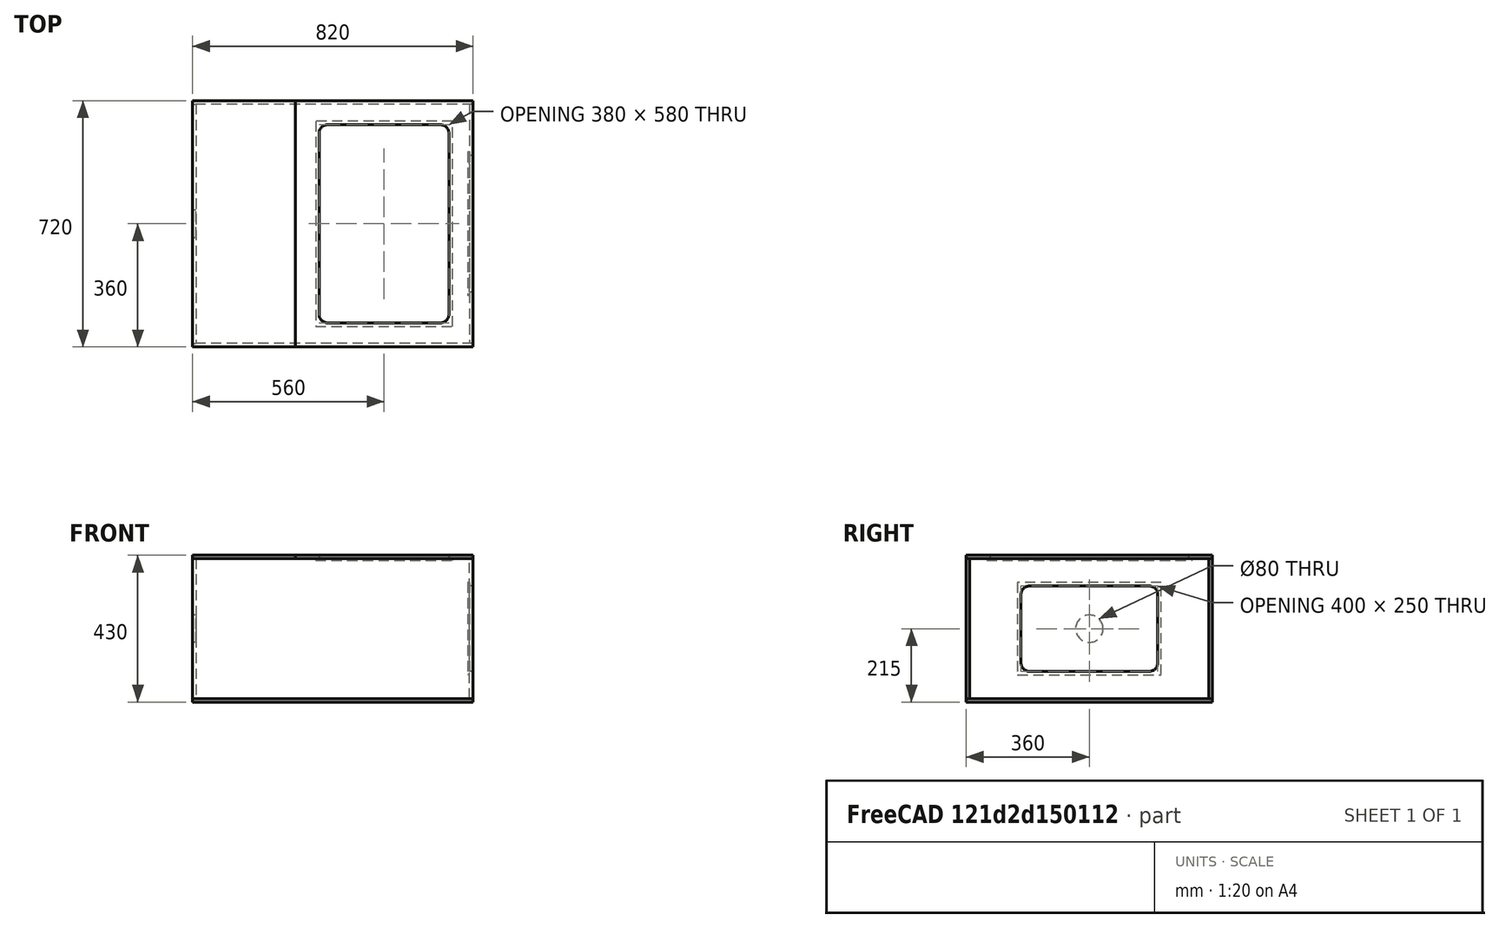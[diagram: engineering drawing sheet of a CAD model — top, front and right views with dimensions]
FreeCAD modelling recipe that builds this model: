
FCSTD DOCUMENT  (FreeCAD 0.19R24276 (Git))
Label: laser_cutter_enclosure
License: All rights reserved
LicenseURL: http://en.wikipedia.org/wiki/All_rights_reserved
objects: TechDraw::DrawProjGroupItem×81, TechDraw::DrawViewDimension×23, Sketcher::SketchObject×12, PartDesign::Pad×9, PartDesign::Body×9, TechDraw::DrawSVGTemplate×9, TechDraw::DrawProjGroup×9, TechDraw::DrawPage×9, PartDesign::ShapeBinder×8, PartDesign::Pocket×3
note: 53 computed .brp shape members not serialized (recipe doc carries the construction recipe); baked Part::Feature solids carry a one-line shape summary decoded from their .brp

FEATURE [Sketcher::SketchObject] Sketch
  FullyConstrained = true
  MapMode = 5
  Support = -> [XY_Plane]
  sketch-geometry (4):
    g0: LineSegment StartX=-410 StartY=360 StartZ=0 EndX=410 EndY=360 EndZ=0
    g1: LineSegment StartX=410 StartY=360 StartZ=0 EndX=410 EndY=-360 EndZ=0
    g2: LineSegment StartX=410 StartY=-360 StartZ=0 EndX=-410 EndY=-360 EndZ=0
    g3: LineSegment StartX=-410 StartY=-360 StartZ=0 EndX=-410 EndY=360 EndZ=0
  constraints (11):
    c: Coincident(g0,g1)
    c: Coincident(g1,g2)
    c: Coincident(g2,g3)
    c: Coincident(g3,g0)
    c: Horizontal(g0)
    c: Horizontal(g2)
    c: Vertical(g1)
    c: Vertical(g3)
    c: Symmetric(g0,g2,g-1)
    c: DistanceX(g0,g0) = 820
    c: DistanceY(g1,g1) = 720
FEATURE [PartDesign::Pad] Pad  label="bottom001"
  Direction = (1,1,1)
  Length = 10
  Length2 = 100
  Profile = -> Sketch
  Type = 0
FEATURE [PartDesign::Body] Body  label="bottom"
  Group = -> [Sketch,Pad]
  Origin = -> Origin
  Tip = -> Pad
FEATURE [PartDesign::ShapeBinder] CopyPad
  Placement = pos=(0,0,10) rot=(0,0,1;0rad)
  TraceSupport = false
FEATURE [Sketcher::SketchObject] Sketch001
  ExternalGeometry = -> [CopyPad]
  FullyConstrained = true
  MapMode = 5
  Placement = pos=(0,0,10) rot=(0,0,1;0rad)
  Support = -> [CopyPad]
  sketch-geometry (4):
    g0: LineSegment StartX=-410 StartY=360 StartZ=0 EndX=410 EndY=360 EndZ=0
    g1: LineSegment StartX=410 StartY=360 StartZ=0 EndX=410 EndY=350 EndZ=0
    g2: LineSegment StartX=410 StartY=350 StartZ=0 EndX=-410 EndY=350 EndZ=0
    g3: LineSegment StartX=-410 StartY=350 StartZ=0 EndX=-410 EndY=360 EndZ=0
  constraints (10):
    c: Coincident(g0,g1)
    c: Coincident(g1,g2)
    c: Coincident(g2,g3)
    c: Coincident(g3,g0)
    c: Horizontal(g2)
    c: Vertical(g1)
    c: Vertical(g3)
    c: Coincident(g0,g-3)
    c: Coincident(g0,g-3)
    c: DistanceY(g1,g1) = 10
FEATURE [PartDesign::Pad] Pad001  label="right_side001"
  Direction = (1,1,1)
  Length = 410
  Length2 = 100
  Placement = pos=(0,0,10) rot=(0,0,1;0rad)
  Profile = -> Sketch001
  Type = 0
FEATURE [PartDesign::Body] Body001  label="right_side"
  Group = -> [CopyPad,Sketch001,Pad001]
  Origin = -> Origin001
  Tip = -> Pad001
FEATURE [PartDesign::ShapeBinder] CopyPad001
  Placement = pos=(0,0,10) rot=(0,0,1;0rad)
  TraceSupport = false
FEATURE [Sketcher::SketchObject] Sketch002
  ExternalGeometry = -> [CopyPad001]
  FullyConstrained = true
  MapMode = 5
  Placement = pos=(0,0,10) rot=(0,0,1;0rad)
  Support = -> [CopyPad001]
  sketch-geometry (4):
    g0: LineSegment StartX=-410 StartY=-360 StartZ=0 EndX=410 EndY=-360 EndZ=0
    g1: LineSegment StartX=410 StartY=-360 StartZ=0 EndX=410 EndY=-350 EndZ=0
    g2: LineSegment StartX=410 StartY=-350 StartZ=0 EndX=-410 EndY=-350 EndZ=0
    g3: LineSegment StartX=-410 StartY=-350 StartZ=0 EndX=-410 EndY=-360 EndZ=0
  constraints (11):
    c: Coincident(g0,g1)
    c: Coincident(g1,g2)
    c: Coincident(g2,g3)
    c: Coincident(g3,g0)
    c: Horizontal(g0)
    c: Horizontal(g2)
    c: Vertical(g1)
    c: Vertical(g3)
    c: Coincident(g0,g-3)
    c: PointOnObject(g1,g-4)
    c: DistanceY(g1,g1) = 10
FEATURE [PartDesign::Pad] Pad002  label="left_side001"
  Direction = (1,1,1)
  Length = 410
  Length2 = 100
  Placement = pos=(0,0,10) rot=(0,0,1;0rad)
  Profile = -> Sketch002
  Type = 0
FEATURE [PartDesign::Body] Body002  label="left_side"
  Group = -> [CopyPad001,Sketch002,Pad002]
  Origin = -> Origin002
  Tip = -> Pad002
FEATURE [PartDesign::ShapeBinder] CopyPad002
  Placement = pos=(0,0,410) rot=(0,0,1;0rad)
  TraceSupport = false
FEATURE [Sketcher::SketchObject] Sketch003
  ExternalGeometry = -> [CopyPad002]
  FullyConstrained = true
  MapMode = 5
  Placement = pos=(0,0,420) rot=(0,0,1;0rad)
  Support = -> [CopyPad002]
  sketch-geometry (4):
    g0: LineSegment StartX=-410 StartY=-360 StartZ=0 EndX=-110 EndY=-360 EndZ=0
    g1: LineSegment StartX=-110 StartY=-360 StartZ=0 EndX=-110 EndY=360 EndZ=0
    g2: LineSegment StartX=-110 StartY=360 StartZ=0 EndX=-410 EndY=360 EndZ=0
    g3: LineSegment StartX=-410 StartY=360 StartZ=0 EndX=-410 EndY=-360 EndZ=0
  constraints (11):
    c: Coincident(g0,g1)
    c: Coincident(g1,g2)
    c: Coincident(g2,g3)
    c: Coincident(g3,g0)
    c: Horizontal(g0)
    c: Horizontal(g2)
    c: Vertical(g1)
    c: Vertical(g3)
    c: Coincident(g0,g-3)
    c: DistanceX(g2,g2) = 300
    c: DistanceY(g1,g1) = 720
FEATURE [PartDesign::Pad] Pad003  label="fixed_top_part001"
  Direction = (1,1,1)
  Length = 10
  Length2 = 100
  Placement = pos=(0,0,410) rot=(0,0,1;0rad)
  Profile = -> Sketch003
  Type = 0
FEATURE [PartDesign::Body] Body003  label="fixed_top_part"
  Group = -> [CopyPad002,Sketch003,Pad003]
  Origin = -> Origin003
  Tip = -> Pad003
FEATURE [PartDesign::ShapeBinder] CopyPad002001
  Placement = pos=(0,0,410) rot=(0,0,1;0rad)
  TraceSupport = false
FEATURE [Sketcher::SketchObject] Sketch004
  ExternalGeometry = -> [CopyPad002001]
  FullyConstrained = true
  MapMode = 5
  Placement = pos=(0,0,420) rot=(0,0,1;0rad)
  Support = -> [CopyPad002001]
  sketch-geometry (4):
    g0: LineSegment StartX=410 StartY=-360 StartZ=0 EndX=-110 EndY=-360 EndZ=0
    g1: LineSegment StartX=-110 StartY=-360 StartZ=0 EndX=-110 EndY=360 EndZ=0
    g2: LineSegment StartX=-110 StartY=360 StartZ=0 EndX=410 EndY=360 EndZ=0
    g3: LineSegment StartX=410 StartY=360 StartZ=0 EndX=410 EndY=-360 EndZ=0
  constraints (11):
    c: Coincident(g0,g1)
    c: Coincident(g1,g2)
    c: Coincident(g2,g3)
    c: Coincident(g3,g0)
    c: Horizontal(g0)
    c: Horizontal(g2)
    c: Vertical(g1)
    c: Vertical(g3)
    c: Coincident(g0,g-3)
    c: DistanceY(g3,g3) = 720
    c: DistanceX(g2,g2) = 520
FEATURE [PartDesign::Pad] Pad004
  Direction = (1,1,1)
  Length = 10
  Length2 = 100
  Placement = pos=(0,0,410) rot=(0,0,1;0rad)
  Profile = -> Sketch004
  Type = 0
FEATURE [PartDesign::ShapeBinder] CopyPad001001
  Placement = pos=(0,0,10) rot=(0,0,1;0rad)
  TraceSupport = false
FEATURE [Sketcher::SketchObject] Sketch005
  ExternalGeometry = -> [CopyPad001001]
  FullyConstrained = true
  MapMode = 5
  Placement = pos=(0,350,10) rot=(1,0,0;1.5708rad)
  Support = -> [CopyPad001001]
  sketch-geometry (4):
    g0: LineSegment StartX=410 StartY=0 StartZ=0 EndX=400 EndY=0 EndZ=0
    g1: LineSegment StartX=400 StartY=0 StartZ=0 EndX=400 EndY=410 EndZ=0
    g2: LineSegment StartX=400 StartY=410 StartZ=0 EndX=410 EndY=410 EndZ=0
    g3: LineSegment StartX=410 StartY=410 StartZ=0 EndX=410 EndY=0 EndZ=0
  constraints (11):
    c: Coincident(g0,g1)
    c: Coincident(g1,g2)
    c: Coincident(g2,g3)
    c: Coincident(g3,g0)
    c: Horizontal(g0)
    c: Horizontal(g2)
    c: Vertical(g1)
    c: Vertical(g3)
    c: Coincident(g0,g-3)
    c: DistanceX(g2,g2) = 10
    c: DistanceY(g3,g3) = 410
FEATURE [PartDesign::Pad] Pad005
  Direction = (1,1,1)
  Length = 700
  Length2 = 100
  Placement = pos=(0,0,10) rot=(0,0,1;0rad)
  Profile = -> Sketch005
  Type = 0
FEATURE [PartDesign::ShapeBinder] CopyPad001002
  Placement = pos=(0,0,10) rot=(0,0,1;0rad)
  TraceSupport = false
FEATURE [Sketcher::SketchObject] Sketch006
  ExternalGeometry = -> [CopyPad001002]
  FullyConstrained = true
  MapMode = 5
  Placement = pos=(0,350,10) rot=(1,0,0;1.5708rad)
  Support = -> [CopyPad001002]
  sketch-geometry (4):
    g0: LineSegment StartX=-410 StartY=410 StartZ=0 EndX=-400 EndY=410 EndZ=0
    g1: LineSegment StartX=-400 StartY=410 StartZ=0 EndX=-400 EndY=0 EndZ=0
    g2: LineSegment StartX=-400 StartY=0 StartZ=0 EndX=-410 EndY=0 EndZ=0
    g3: LineSegment StartX=-410 StartY=0 StartZ=0 EndX=-410 EndY=410 EndZ=0
  constraints (11):
    c: Coincident(g0,g1)
    c: Coincident(g1,g2)
    c: Coincident(g2,g3)
    c: Coincident(g3,g0)
    c: Horizontal(g0)
    c: Horizontal(g2)
    c: Vertical(g1)
    c: Vertical(g3)
    c: Coincident(g0,g-3)
    c: DistanceX(g2,g2) = 10
    c: DistanceY(g3,g3) = 410
FEATURE [PartDesign::Pad] Pad006  label="back_side001"
  Direction = (1,1,1)
  Length = 700
  Length2 = 100
  Placement = pos=(0,0,10) rot=(0,0,1;0rad)
  Profile = -> Sketch006
  Type = 0
FEATURE [Sketcher::SketchObject] Sketch007
  ExternalGeometry = -> [Pad004]
  FullyConstrained = true
  MapMode = 5
  Placement = pos=(0,0,430) rot=(0,0,1;0rad)
  Support = -> [Pad004]
  sketch-geometry (14):
    g0: LineSegment StartX=150 StartY=360 StartZ=0 EndX=150 EndY=-360 EndZ=0
    g1: LineSegment StartX=-110 StartY=9e-15 StartZ=0 EndX=410 EndY=9e-15 EndZ=0
    g2: LineSegment StartX=-15 StartY=290 StartZ=0 EndX=315 EndY=290 EndZ=0
    g3: LineSegment StartX=340 StartY=265 StartZ=0 EndX=340 EndY=-265 EndZ=0
    g4: LineSegment StartX=315 StartY=-290 StartZ=0 EndX=-15 EndY=-290 EndZ=0
    g5: LineSegment StartX=-40 StartY=-265 StartZ=0 EndX=-40 EndY=265 EndZ=0
    g6: ArcOfCircle CenterX=-15 CenterY=265 CenterZ=0 NormalX=0 NormalY=0 NormalZ=1 AngleXU=0 Radius=25 StartAngle=1.5708 EndAngle=3.14159
    g7: ArcOfCircle CenterX=-15 CenterY=-265 CenterZ=0 NormalX=0 NormalY=0 NormalZ=1 AngleXU=0 Radius=25 StartAngle=3.14159 EndAngle=4.71239
    g8: ArcOfCircle CenterX=315 CenterY=-265 CenterZ=0 NormalX=0 NormalY=0 NormalZ=1 AngleXU=0 Radius=25 StartAngle=4.71239 EndAngle=6.28319
    g9: ArcOfCircle CenterX=315 CenterY=265 CenterZ=0 NormalX=0 NormalY=0 NormalZ=1 AngleXU=0 Radius=25 StartAngle=9e-16 EndAngle=1.5708
    g10: LineSegment StartX=-15 StartY=265 StartZ=0 EndX=315 EndY=265 EndZ=0
    g11: LineSegment StartX=315 StartY=265 StartZ=0 EndX=315 EndY=-265 EndZ=0
    g12: LineSegment StartX=315 StartY=-265 StartZ=0 EndX=-15 EndY=-265 EndZ=0
    g13: LineSegment StartX=-15 StartY=-265 StartZ=0 EndX=-15 EndY=265 EndZ=0
  constraints (32):
    c: PointOnObject(g0,g-5)
    c: Vertical(g0)
    c: PointOnObject(g1,g-6)
    c: Horizontal(g1)
    c: Symmetric(g-4,g-5,g1)
    c: Symmetric(g-6,g-4,g0)
    c: Horizontal(g2)
    c: Horizontal(g4)
    c: Vertical(g3)
    c: Vertical(g5)
    c: Tangent(g2,g6) = 1.5708
    c: Tangent(g5,g6) = 1.5708
    c: Tangent(g5,g7) = 1.5708
    c: Tangent(g4,g7) = 1.5708
    c: Tangent(g4,g8) = 1.5708
    c: Tangent(g3,g8) = 1.5708
    c: Tangent(g3,g9) = 1.5708
    c: Tangent(g2,g9) = 1.5708
    c: Coincident(g10,g11)
    c: Coincident(g11,g12)
    c: Coincident(g12,g13)
    c: Coincident(g13,g10)
    c: Horizontal(g12)
    c: Coincident(g10,g6)
    c: Coincident(g8,g11)
    c: Coincident(g12,g7)
    c: Coincident(g9,g10)
    c: Radius(g8) = 25
    c: Symmetric(g8,g9,g1)
    c: DistanceX(g5,g3) = 380
    c: DistanceY(g4,g2) = 580
    c: Symmetric(g6,g9,g0)
FEATURE [PartDesign::Pocket] Pocket  label="top_door001"
  BaseFeature = -> Pad004
  Length = 10
  Length2 = 100
  Placement = pos=(0,0,410) rot=(0,0,1;0rad)
  Profile = -> Sketch007
  Type = 0
FEATURE [PartDesign::Body] Body004  label="top_door"
  Group = -> [CopyPad002001,Sketch004,Pad004,Sketch007,Pocket]
  Origin = -> Origin004
  Tip = -> Pocket
FEATURE [Sketcher::SketchObject] Sketch008
  ExternalGeometry = -> [Pad005]
  FullyConstrained = true
  MapMode = 5
  Placement = pos=(410,0,10) rot=(0.57735,0.57735,0.57735;2.0944rad)
  Support = -> [Pad005]
  sketch-geometry (13):
    g0: LineSegment StartX=-175 StartY=305 StartZ=0 EndX=175 EndY=305 EndZ=0
    g1: LineSegment StartX=175 StartY=305 StartZ=0 EndX=175 EndY=105 EndZ=0
    g2: LineSegment StartX=175 StartY=105 StartZ=0 EndX=-175 EndY=105 EndZ=0
    g3: LineSegment StartX=-175 StartY=105 StartZ=0 EndX=-175 EndY=305 EndZ=0
    g4: LineSegment StartX=-175 StartY=330 StartZ=0 EndX=175 EndY=330 EndZ=0
    g5: LineSegment StartX=200 StartY=305 StartZ=0 EndX=200 EndY=105 EndZ=0
    g6: LineSegment StartX=175 StartY=80 StartZ=0 EndX=-175 EndY=80 EndZ=0
    g7: LineSegment StartX=-200 StartY=105 StartZ=0 EndX=-200 EndY=305 EndZ=0
    g8: ArcOfCircle CenterX=-175 CenterY=305 CenterZ=0 NormalX=0 NormalY=0 NormalZ=1 AngleXU=0 Radius=25 StartAngle=1.5708 EndAngle=3.14159
    g9: ArcOfCircle CenterX=-175 CenterY=105 CenterZ=0 NormalX=0 NormalY=0 NormalZ=1 AngleXU=0 Radius=25 StartAngle=3.14159 EndAngle=4.71239
    g10: ArcOfCircle CenterX=175 CenterY=105 CenterZ=0 NormalX=0 NormalY=0 NormalZ=1 AngleXU=0 Radius=25 StartAngle=4.71239 EndAngle=6.28319
    g11: ArcOfCircle CenterX=175 CenterY=305 CenterZ=0 NormalX=0 NormalY=0 NormalZ=1 AngleXU=0 Radius=25 StartAngle=-9e-16 EndAngle=1.5708
    g12: LineSegment StartX=-350 StartY=205 StartZ=0 EndX=350 EndY=205 EndZ=0
  constraints (29):
    c: Coincident(g0,g1)
    c: Coincident(g1,g2)
    c: Coincident(g2,g3)
    c: Coincident(g3,g0)
    c: Horizontal(g2)
    c: Vertical(g1)
    c: Vertical(g3)
    c: Horizontal(g4)
    c: Horizontal(g6)
    c: Vertical(g5)
    c: Tangent(g4,g8) = 1.5708
    c: Tangent(g7,g8) = 1.5708
    c: Tangent(g6,g9) = 1.5708
    c: Tangent(g7,g9) = 1.5708
    c: Tangent(g6,g10) = 1.5708
    c: Tangent(g5,g10) = 1.5708
    c: Tangent(g4,g11) = 1.5708
    c: Tangent(g5,g11) = 1.5708
    c: Symmetric(g0,g0,g-2)
    c: PointOnObject(g12,g-4)
    c: Symmetric(g-5,g-6,g12)
    c: Coincident(g8,g0)
    c: Coincident(g9,g2)
    c: Coincident(g10,g1)
    c: Coincident(g11,g0)
    c: Radius(g8) = 25
    c: DistanceX(g-4,g7) = 150
    c: Symmetric(g10,g11,g12)
    c: DistanceY(g4,g-5) = 80
FEATURE [PartDesign::Pocket] Pocket001  label="front_door001"
  BaseFeature = -> Pad005
  Length = 10
  Length2 = 100
  Placement = pos=(0,0,10) rot=(0,0,1;0rad)
  Profile = -> Sketch008
  Type = 0
FEATURE [PartDesign::Body] Body005  label="front_door"
  Group = -> [CopyPad001001,Sketch005,Pad005,Sketch008,Pocket001]
  Origin = -> Origin005
  Tip = -> Pocket001
FEATURE [PartDesign::ShapeBinder] CopyPocket
  Placement = pos=(0,0,410) rot=(0,0,1;0rad)
  TraceSupport = false
FEATURE [Sketcher::SketchObject] Sketch009
  ExternalGeometry = -> [CopyPocket]
  FullyConstrained = true
  MapMode = 5
  Placement = pos=(0,0,420) rot=(1,0,0;3.14159rad)
  Support = -> [CopyPocket]
  sketch-geometry (4):
    g0: LineSegment StartX=-50 StartY=300 StartZ=0 EndX=350 EndY=300 EndZ=0
    g1: LineSegment StartX=350 StartY=300 StartZ=0 EndX=350 EndY=-300 EndZ=0
    g2: LineSegment StartX=350 StartY=-300 StartZ=0 EndX=-50 EndY=-300 EndZ=0
    g3: LineSegment StartX=-50 StartY=-300 StartZ=0 EndX=-50 EndY=300 EndZ=0
  constraints (12):
    c: Coincident(g0,g1)
    c: Coincident(g1,g2)
    c: Coincident(g2,g3)
    c: Coincident(g3,g0)
    c: Horizontal(g0)
    c: Horizontal(g2)
    c: Vertical(g1)
    c: Vertical(g3)
    c: DistanceX(g0,g-5) = 10
    c: DistanceY(g-3,g0) = 10
    c: DistanceX(g-6,g1) = 10
    c: DistanceY(g1,g-4) = 10
FEATURE [PartDesign::Pad] Pad007  label="top_glass001"
  Direction = (1,1,1)
  Length = 5
  Length2 = 100
  Placement = pos=(0,0,410) rot=(0,0,1;0rad)
  Profile = -> Sketch009
  Type = 0
FEATURE [PartDesign::Body] Body007  label="top_glass"
  Group = -> [CopyPocket,Sketch009,Pad007]
  Origin = -> Origin007
  Tip = -> Pad007
FEATURE [PartDesign::ShapeBinder] CopyPocket001
  Placement = pos=(0,0,10) rot=(0,0,1;0rad)
  TraceSupport = false
FEATURE [Sketcher::SketchObject] Sketch010
  ExternalGeometry = -> [CopyPocket001]
  FullyConstrained = true
  MapMode = 5
  Placement = pos=(400,0,10) rot=(0.57735,-0.57735,-0.57735;2.0944rad)
  Support = -> [CopyPocket001]
  sketch-geometry (4):
    g0: LineSegment StartX=-210 StartY=340 StartZ=0 EndX=210 EndY=340 EndZ=0
    g1: LineSegment StartX=210 StartY=340 StartZ=0 EndX=210 EndY=70 EndZ=0
    g2: LineSegment StartX=210 StartY=70 StartZ=0 EndX=-210 EndY=70 EndZ=0
    g3: LineSegment StartX=-210 StartY=70 StartZ=0 EndX=-210 EndY=340 EndZ=0
  constraints (12):
    c: Coincident(g0,g1)
    c: Coincident(g1,g2)
    c: Coincident(g2,g3)
    c: Coincident(g3,g0)
    c: Horizontal(g0)
    c: Horizontal(g2)
    c: Vertical(g1)
    c: Vertical(g3)
    c: DistanceY(g-3,g0) = 10
    c: DistanceX(g0,g-4) = 10
    c: DistanceX(g-6,g1) = 10
    c: DistanceY(g1,g-5) = 10
FEATURE [PartDesign::Pad] Pad008  label="front_glass001"
  Direction = (1,1,1)
  Length = 5
  Length2 = 100
  Placement = pos=(0,0,10) rot=(0,0,1;0rad)
  Profile = -> Sketch010
  Type = 0
FEATURE [PartDesign::Body] Body008  label="front_glass"
  Group = -> [CopyPocket001,Sketch010,Pad008]
  Origin = -> Origin008
  Tip = -> Pad008
FEATURE [TechDraw::DrawSVGTemplate] Template_bottom001
  Height = 210
  Orientation = 1
  Width = 297
FEATURE [TechDraw::DrawProjGroupItem] ProjItem  label="Front"
  CoarseView = false
  Direction = (0,-1,0)
  Focus = 100
  HardHidden = false
  IsoCount = 0
  IsoHidden = false
  IsoVisible = false
  LockPosition = true
  Perspective = false
  Rotation = 0
  RotationVector = (1,0,0)
  Scale = 0.05
  ScaleType = 2
  SeamHidden = false
  SeamVisible = true
  SmoothHidden = false
  SmoothVisible = true
  Source = -> [Pad]
  Type = 0
  X = 0
  XDirection = (1,0,0)
  Y = 0
FEATURE [TechDraw::DrawProjGroupItem] ProjItem001  label="Right"
  CoarseView = false
  Direction = (1,-1e-16,0)
  Focus = 100
  HardHidden = false
  IsoCount = 0
  IsoHidden = false
  IsoVisible = false
  LockPosition = false
  Perspective = false
  Rotation = 0
  RotationVector = (1,0,0)
  Scale = 0.05
  ScaleType = 2
  SeamHidden = false
  SeamVisible = true
  SmoothHidden = false
  SmoothVisible = true
  Source = -> [Pad]
  Type = 2
  X = -60.2236
  XDirection = (1e-16,1,0)
  Y = 0
FEATURE [TechDraw::DrawProjGroupItem] ProjItem002  label="Top"
  CoarseView = false
  Direction = (0,0,1)
  Focus = 100
  HardHidden = false
  IsoCount = 0
  IsoHidden = false
  IsoVisible = false
  LockPosition = false
  Perspective = false
  Rotation = 0
  RotationVector = (1,0,0)
  Scale = 0.05
  ScaleType = 2
  SeamHidden = false
  SeamVisible = true
  SmoothHidden = false
  SmoothVisible = true
  Source = -> [Pad]
  Type = 4
  X = 0
  XDirection = (1,0,0)
  Y = -78.6708
FEATURE [TechDraw::DrawProjGroupItem] ProjItem003  label="Left"
  CoarseView = false
  Direction = (-1,-1e-16,0)
  Focus = 100
  HardHidden = false
  IsoCount = 0
  IsoHidden = false
  IsoVisible = false
  LockPosition = false
  Perspective = false
  Rotation = 0
  RotationVector = (1,0,0)
  Scale = 0.05
  ScaleType = 2
  SeamHidden = false
  SeamVisible = true
  SmoothHidden = false
  SmoothVisible = true
  Source = -> [Pad]
  Type = 1
  X = 60.2236
  XDirection = (1e-16,-1,0)
  Y = 0
FEATURE [TechDraw::DrawProjGroupItem] ProjItem004  label="Bottom"
  CoarseView = false
  Direction = (0,0,-1)
  Focus = 100
  HardHidden = false
  IsoCount = 0
  IsoHidden = false
  IsoVisible = false
  LockPosition = false
  Perspective = false
  Rotation = 0
  RotationVector = (1,0,0)
  Scale = 0.05
  ScaleType = 2
  SeamHidden = false
  SeamVisible = true
  SmoothHidden = false
  SmoothVisible = true
  Source = -> [Pad]
  Type = 5
  X = 0
  XDirection = (1,0,0)
  Y = 60.2236
FEATURE [TechDraw::DrawProjGroupItem] ProjItem005  label="FrontBottomLeft"
  CoarseView = false
  Direction = (-0.57735,-0.57735,-0.57735)
  Focus = 100
  HardHidden = false
  IsoCount = 0
  IsoHidden = false
  IsoVisible = false
  LockPosition = false
  Perspective = false
  Rotation = 0
  RotationVector = (1,0,0)
  Scale = 0.05
  ScaleType = 2
  SeamHidden = false
  SeamVisible = true
  SmoothHidden = false
  SmoothVisible = true
  Source = -> [Pad]
  Type = 8
  X = 69.4472
  XDirection = (0.707107,-0.707107,0)
  Y = 58.1453
FEATURE [TechDraw::DrawProjGroupItem] ProjItem006  label="FrontTopRight"
  CoarseView = false
  Direction = (0.57735,-0.57735,0.57735)
  Focus = 100
  HardHidden = false
  IsoCount = 0
  IsoHidden = false
  IsoVisible = false
  LockPosition = false
  Perspective = false
  Rotation = 0
  RotationVector = (1,0,0)
  Scale = 0.05
  ScaleType = 2
  SeamHidden = false
  SeamVisible = true
  SmoothHidden = false
  SmoothVisible = true
  Source = -> [Pad]
  Type = 7
  X = -69.4472
  XDirection = (0.707107,0.707107,0)
  Y = -80.7492
FEATURE [TechDraw::DrawProjGroupItem] ProjItem007  label="FrontTopLeft"
  CoarseView = false
  Direction = (-0.57735,-0.57735,0.57735)
  Focus = 100
  HardHidden = false
  IsoCount = 0
  IsoHidden = false
  IsoVisible = false
  LockPosition = false
  Perspective = false
  Rotation = 0
  RotationVector = (1,0,0)
  Scale = 0.05
  ScaleType = 2
  SeamHidden = false
  SeamVisible = true
  SmoothHidden = false
  SmoothVisible = true
  Source = -> [Pad]
  Type = 6
  X = 69.4472
  XDirection = (0.707107,-0.707107,0)
  Y = -80.7492
FEATURE [TechDraw::DrawProjGroupItem] ProjItem008  label="FrontBottomRight"
  CoarseView = false
  Direction = (0.57735,-0.57735,-0.57735)
  Focus = 100
  HardHidden = false
  IsoCount = 0
  IsoHidden = false
  IsoVisible = false
  LockPosition = false
  Perspective = false
  Rotation = 0
  RotationVector = (1,0,0)
  Scale = 0.05
  ScaleType = 2
  SeamHidden = false
  SeamVisible = true
  SmoothHidden = false
  SmoothVisible = true
  Source = -> [Pad]
  Type = 9
  X = -69.4472
  XDirection = (0.707107,0.707107,0)
  Y = 58.1453
FEATURE [TechDraw::DrawProjGroup] ProjGroup_bottom001
  Anchor = -> ProjItem
  AutoDistribute = true
  LockPosition = false
  ProjectionType = 0
  Rotation = 0
  Scale = 0.05
  ScaleType = 1
  Source = -> [Pad]
  Views = -> [ProjItem,ProjItem001,ProjItem002,ProjItem003,ProjItem004,ProjItem005,ProjItem006,ProjItem007,ProjItem008]
  X = 148.5
  Y = 105
  spacingX = 15
  spacingY = 15
FEATURE [TechDraw::DrawSVGTemplate] Template_right_side001
  Height = 210
  Orientation = 1
  Width = 297
FEATURE [TechDraw::DrawProjGroupItem] ProjItem009  label="Front001"
  CoarseView = false
  Direction = (0,-1,0)
  Focus = 100
  HardHidden = false
  IsoCount = 0
  IsoHidden = false
  IsoVisible = false
  LockPosition = true
  Perspective = false
  Rotation = 0
  RotationVector = (1,0,0)
  Scale = 0.05
  ScaleType = 2
  SeamHidden = false
  SeamVisible = true
  SmoothHidden = false
  SmoothVisible = true
  Source = -> [Pad001]
  Type = 0
  X = 0
  XDirection = (1,0,0)
  Y = 0
FEATURE [TechDraw::DrawProjGroupItem] ProjItem010  label="Right001"
  CoarseView = false
  Direction = (1,-1e-16,0)
  Focus = 100
  HardHidden = false
  IsoCount = 0
  IsoHidden = false
  IsoVisible = false
  LockPosition = false
  Perspective = false
  Rotation = 0
  RotationVector = (1,0,0)
  Scale = 0.05
  ScaleType = 2
  SeamHidden = false
  SeamVisible = true
  SmoothHidden = false
  SmoothVisible = true
  Source = -> [Pad001]
  Type = 2
  X = -35.75
  XDirection = (1e-16,1,0)
  Y = 0
FEATURE [TechDraw::DrawProjGroupItem] ProjItem011  label="Top001"
  CoarseView = false
  Direction = (0,0,1)
  Focus = 100
  HardHidden = false
  IsoCount = 0
  IsoHidden = false
  IsoVisible = false
  LockPosition = false
  Perspective = false
  Rotation = 0
  RotationVector = (1,0,0)
  Scale = 0.05
  ScaleType = 2
  SeamHidden = false
  SeamVisible = true
  SmoothHidden = false
  SmoothVisible = true
  Source = -> [Pad001]
  Type = 4
  X = 0
  XDirection = (1,0,0)
  Y = -76.25
FEATURE [TechDraw::DrawProjGroupItem] ProjItem012  label="Left001"
  CoarseView = false
  Direction = (-1,-1e-16,0)
  Focus = 100
  HardHidden = false
  IsoCount = 0
  IsoHidden = false
  IsoVisible = false
  LockPosition = false
  Perspective = false
  Rotation = 0
  RotationVector = (1,0,0)
  Scale = 0.05
  ScaleType = 2
  SeamHidden = false
  SeamVisible = true
  SmoothHidden = false
  SmoothVisible = true
  Source = -> [Pad001]
  Type = 1
  X = 35.75
  XDirection = (1e-16,-1,0)
  Y = 0
FEATURE [TechDraw::DrawProjGroupItem] ProjItem013  label="Bottom001"
  CoarseView = false
  Direction = (0,0,-1)
  Focus = 100
  HardHidden = false
  IsoCount = 0
  IsoHidden = false
  IsoVisible = false
  LockPosition = false
  Perspective = false
  Rotation = 0
  RotationVector = (1,0,0)
  Scale = 0.05
  ScaleType = 2
  SeamHidden = false
  SeamVisible = true
  SmoothHidden = false
  SmoothVisible = true
  Source = -> [Pad001]
  Type = 5
  X = 0
  XDirection = (1,0,0)
  Y = 35.75
FEATURE [TechDraw::DrawProjGroupItem] ProjItem014  label="FrontBottomLeft001"
  CoarseView = false
  Direction = (-0.57735,-0.57735,-0.57735)
  Focus = 100
  HardHidden = false
  IsoCount = 0
  IsoHidden = false
  IsoVisible = false
  LockPosition = false
  Perspective = false
  Rotation = 0
  RotationVector = (1,0,0)
  Scale = 0.05
  ScaleType = 2
  SeamHidden = false
  SeamVisible = true
  SmoothHidden = false
  SmoothVisible = true
  Source = -> [Pad001]
  Type = 8
  X = 50.1725
  XDirection = (0.707107,-0.707107,0)
  Y = 52.3402
FEATURE [TechDraw::DrawProjGroupItem] ProjItem015  label="FrontTopRight001"
  CoarseView = false
  Direction = (0.57735,-0.57735,0.57735)
  Focus = 100
  HardHidden = false
  IsoCount = 0
  IsoHidden = false
  IsoVisible = false
  LockPosition = false
  Perspective = false
  Rotation = 0
  RotationVector = (1,0,0)
  Scale = 0.05
  ScaleType = 2
  SeamHidden = false
  SeamVisible = true
  SmoothHidden = false
  SmoothVisible = true
  Source = -> [Pad001]
  Type = 7
  X = -50.1725
  XDirection = (0.707107,0.707107,0)
  Y = -59.6598
FEATURE [TechDraw::DrawProjGroupItem] ProjItem016  label="FrontTopLeft001"
  CoarseView = false
  Direction = (-0.57735,-0.57735,0.57735)
  Focus = 100
  HardHidden = false
  IsoCount = 0
  IsoHidden = false
  IsoVisible = false
  LockPosition = false
  Perspective = false
  Rotation = 0
  RotationVector = (1,0,0)
  Scale = 0.05
  ScaleType = 2
  SeamHidden = false
  SeamVisible = true
  SmoothHidden = false
  SmoothVisible = true
  Source = -> [Pad001]
  Type = 6
  X = 50.1725
  XDirection = (0.707107,-0.707107,0)
  Y = -59.6598
FEATURE [TechDraw::DrawProjGroupItem] ProjItem017  label="FrontBottomRight001"
  CoarseView = false
  Direction = (0.57735,-0.57735,-0.57735)
  Focus = 100
  HardHidden = false
  IsoCount = 0
  IsoHidden = false
  IsoVisible = false
  LockPosition = false
  Perspective = false
  Rotation = 0
  RotationVector = (1,0,0)
  Scale = 0.05
  ScaleType = 2
  SeamHidden = false
  SeamVisible = true
  SmoothHidden = false
  SmoothVisible = true
  Source = -> [Pad001]
  Type = 9
  X = -50.1725
  XDirection = (0.707107,0.707107,0)
  Y = 52.3402
FEATURE [TechDraw::DrawProjGroup] ProjGroup_right_side001
  Anchor = -> ProjItem009
  AutoDistribute = true
  LockPosition = false
  ProjectionType = 0
  Rotation = 0
  Scale = 0.05
  ScaleType = 1
  Source = -> [Pad001]
  Views = -> [ProjItem009,ProjItem010,ProjItem011,ProjItem012,ProjItem013,ProjItem014,ProjItem015,ProjItem016,ProjItem017]
  X = 148.5
  Y = 105
  spacingX = 15
  spacingY = 15
FEATURE [TechDraw::DrawSVGTemplate] Template_left_side001
  Height = 210
  Orientation = 1
  Width = 297
FEATURE [TechDraw::DrawProjGroupItem] ProjItem018  label="Front002"
  CoarseView = false
  Direction = (0,-1,0)
  Focus = 100
  HardHidden = false
  IsoCount = 0
  IsoHidden = false
  IsoVisible = false
  LockPosition = true
  Perspective = false
  Rotation = 0
  RotationVector = (1,0,0)
  Scale = 0.05
  ScaleType = 2
  SeamHidden = false
  SeamVisible = true
  SmoothHidden = false
  SmoothVisible = true
  Source = -> [Pad002]
  Type = 0
  X = 0
  XDirection = (1,0,0)
  Y = 0
FEATURE [TechDraw::DrawProjGroupItem] ProjItem019  label="Right002"
  CoarseView = false
  Direction = (1,-1e-16,0)
  Focus = 100
  HardHidden = false
  IsoCount = 0
  IsoHidden = false
  IsoVisible = false
  LockPosition = false
  Perspective = false
  Rotation = 0
  RotationVector = (1,0,0)
  Scale = 0.05
  ScaleType = 2
  SeamHidden = false
  SeamVisible = true
  SmoothHidden = false
  SmoothVisible = true
  Source = -> [Pad002]
  Type = 2
  X = -35.75
  XDirection = (1e-16,1,0)
  Y = 0
FEATURE [TechDraw::DrawProjGroupItem] ProjItem020  label="Top002"
  CoarseView = false
  Direction = (0,0,1)
  Focus = 100
  HardHidden = false
  IsoCount = 0
  IsoHidden = false
  IsoVisible = false
  LockPosition = false
  Perspective = false
  Rotation = 0
  RotationVector = (1,0,0)
  Scale = 0.05
  ScaleType = 2
  SeamHidden = false
  SeamVisible = true
  SmoothHidden = false
  SmoothVisible = true
  Source = -> [Pad002]
  Type = 4
  X = 0
  XDirection = (1,0,0)
  Y = -76.25
FEATURE [TechDraw::DrawProjGroupItem] ProjItem021  label="Left002"
  CoarseView = false
  Direction = (-1,-1e-16,0)
  Focus = 100
  HardHidden = false
  IsoCount = 0
  IsoHidden = false
  IsoVisible = false
  LockPosition = false
  Perspective = false
  Rotation = 0
  RotationVector = (1,0,0)
  Scale = 0.05
  ScaleType = 2
  SeamHidden = false
  SeamVisible = true
  SmoothHidden = false
  SmoothVisible = true
  Source = -> [Pad002]
  Type = 1
  X = 35.75
  XDirection = (1e-16,-1,0)
  Y = 0
FEATURE [TechDraw::DrawProjGroupItem] ProjItem022  label="Bottom002"
  CoarseView = false
  Direction = (0,0,-1)
  Focus = 100
  HardHidden = false
  IsoCount = 0
  IsoHidden = false
  IsoVisible = false
  LockPosition = false
  Perspective = false
  Rotation = 0
  RotationVector = (1,0,0)
  Scale = 0.05
  ScaleType = 2
  SeamHidden = false
  SeamVisible = true
  SmoothHidden = false
  SmoothVisible = true
  Source = -> [Pad002]
  Type = 5
  X = 0
  XDirection = (1,0,0)
  Y = 35.75
FEATURE [TechDraw::DrawProjGroupItem] ProjItem023  label="FrontBottomLeft002"
  CoarseView = false
  Direction = (-0.57735,-0.57735,-0.57735)
  Focus = 100
  HardHidden = false
  IsoCount = 0
  IsoHidden = false
  IsoVisible = false
  LockPosition = false
  Perspective = false
  Rotation = 0
  RotationVector = (1,0,0)
  Scale = 0.05
  ScaleType = 2
  SeamHidden = false
  SeamVisible = true
  SmoothHidden = false
  SmoothVisible = true
  Source = -> [Pad002]
  Type = 8
  X = 50.1725
  XDirection = (0.707107,-0.707107,0)
  Y = 52.3402
FEATURE [TechDraw::DrawProjGroupItem] ProjItem024  label="FrontTopRight002"
  CoarseView = false
  Direction = (0.57735,-0.57735,0.57735)
  Focus = 100
  HardHidden = false
  IsoCount = 0
  IsoHidden = false
  IsoVisible = false
  LockPosition = false
  Perspective = false
  Rotation = 0
  RotationVector = (1,0,0)
  Scale = 0.05
  ScaleType = 2
  SeamHidden = false
  SeamVisible = true
  SmoothHidden = false
  SmoothVisible = true
  Source = -> [Pad002]
  Type = 7
  X = -50.1725
  XDirection = (0.707107,0.707107,0)
  Y = -59.6598
FEATURE [TechDraw::DrawProjGroupItem] ProjItem025  label="FrontTopLeft002"
  CoarseView = false
  Direction = (-0.57735,-0.57735,0.57735)
  Focus = 100
  HardHidden = false
  IsoCount = 0
  IsoHidden = false
  IsoVisible = false
  LockPosition = false
  Perspective = false
  Rotation = 0
  RotationVector = (1,0,0)
  Scale = 0.05
  ScaleType = 2
  SeamHidden = false
  SeamVisible = true
  SmoothHidden = false
  SmoothVisible = true
  Source = -> [Pad002]
  Type = 6
  X = 50.1725
  XDirection = (0.707107,-0.707107,0)
  Y = -59.6598
FEATURE [TechDraw::DrawProjGroupItem] ProjItem026  label="FrontBottomRight002"
  CoarseView = false
  Direction = (0.57735,-0.57735,-0.57735)
  Focus = 100
  HardHidden = false
  IsoCount = 0
  IsoHidden = false
  IsoVisible = false
  LockPosition = false
  Perspective = false
  Rotation = 0
  RotationVector = (1,0,0)
  Scale = 0.05
  ScaleType = 2
  SeamHidden = false
  SeamVisible = true
  SmoothHidden = false
  SmoothVisible = true
  Source = -> [Pad002]
  Type = 9
  X = -50.1725
  XDirection = (0.707107,0.707107,0)
  Y = 52.3402
FEATURE [TechDraw::DrawProjGroup] ProjGroup_left_side001
  Anchor = -> ProjItem018
  AutoDistribute = true
  LockPosition = false
  ProjectionType = 0
  Rotation = 0
  Scale = 0.05
  ScaleType = 1
  Source = -> [Pad002]
  Views = -> [ProjItem018,ProjItem019,ProjItem020,ProjItem021,ProjItem022,ProjItem023,ProjItem024,ProjItem025,ProjItem026]
  X = 148.5
  Y = 105
  spacingX = 15
  spacingY = 15
FEATURE [TechDraw::DrawSVGTemplate] Template_fixed_top_part001
  Height = 210
  Orientation = 1
  Width = 297
FEATURE [TechDraw::DrawProjGroupItem] ProjItem027  label="Front003"
  CoarseView = false
  Direction = (0,-1,0)
  Focus = 100
  HardHidden = false
  IsoCount = 0
  IsoHidden = false
  IsoVisible = false
  LockPosition = true
  Perspective = false
  Rotation = 0
  RotationVector = (1,0,0)
  Scale = 0.075
  ScaleType = 2
  SeamHidden = false
  SeamVisible = true
  SmoothHidden = false
  SmoothVisible = true
  Source = -> [Pad003]
  Type = 0
  X = 0
  XDirection = (1,0,0)
  Y = 0
FEATURE [TechDraw::DrawProjGroupItem] ProjItem028  label="Right003"
  CoarseView = false
  Direction = (1,-1e-16,0)
  Focus = 100
  HardHidden = false
  IsoCount = 0
  IsoHidden = false
  IsoVisible = false
  LockPosition = false
  Perspective = false
  Rotation = 0
  RotationVector = (1,0,0)
  Scale = 0.075
  ScaleType = 2
  SeamHidden = false
  SeamVisible = true
  SmoothHidden = false
  SmoothVisible = true
  Source = -> [Pad003]
  Type = 2
  X = -69.0468
  XDirection = (1e-16,1,0)
  Y = 0
FEATURE [TechDraw::DrawProjGroupItem] ProjItem029  label="Top003"
  CoarseView = false
  Direction = (0,0,1)
  Focus = 100
  HardHidden = false
  IsoCount = 0
  IsoHidden = false
  IsoVisible = false
  LockPosition = false
  Perspective = false
  Rotation = 0
  RotationVector = (1,0,0)
  Scale = 0.075
  ScaleType = 2
  SeamHidden = false
  SeamVisible = true
  SmoothHidden = false
  SmoothVisible = true
  Source = -> [Pad003]
  Type = 4
  X = 0
  XDirection = (1,0,0)
  Y = -69.1405
FEATURE [TechDraw::DrawProjGroupItem] ProjItem030  label="Left003"
  CoarseView = false
  Direction = (-1,-1e-16,0)
  Focus = 100
  HardHidden = false
  IsoCount = 0
  IsoHidden = false
  IsoVisible = false
  LockPosition = false
  Perspective = false
  Rotation = 0
  RotationVector = (1,0,0)
  Scale = 0.075
  ScaleType = 2
  SeamHidden = false
  SeamVisible = true
  SmoothHidden = false
  SmoothVisible = true
  Source = -> [Pad003]
  Type = 1
  X = 69.0468
  XDirection = (1e-16,-1,0)
  Y = 0
FEATURE [TechDraw::DrawProjGroupItem] ProjItem031  label="Bottom003"
  CoarseView = false
  Direction = (0,0,-1)
  Focus = 100
  HardHidden = false
  IsoCount = 0
  IsoHidden = false
  IsoVisible = false
  LockPosition = false
  Perspective = false
  Rotation = 0
  RotationVector = (1,0,0)
  Scale = 0.075
  ScaleType = 2
  SeamHidden = false
  SeamVisible = true
  SmoothHidden = false
  SmoothVisible = true
  Source = -> [Pad003]
  Type = 5
  X = 0
  XDirection = (1,0,0)
  Y = 69.0468
FEATURE [TechDraw::DrawProjGroupItem] ProjItem032  label="FrontBottomLeft003"
  CoarseView = false
  Direction = (-0.57735,-0.57735,-0.57735)
  Focus = 100
  HardHidden = false
  IsoCount = 0
  IsoHidden = false
  IsoVisible = false
  LockPosition = false
  Perspective = false
  Rotation = 0
  RotationVector = (1,0,0)
  Scale = 0.075
  ScaleType = 2
  SeamHidden = false
  SeamVisible = true
  SmoothHidden = false
  SmoothVisible = true
  Source = -> [Pad003]
  Type = 8
  X = 69.0937
  XDirection = (0.707107,-0.707107,0)
  Y = 57.9685
FEATURE [TechDraw::DrawProjGroupItem] ProjItem033  label="FrontTopRight003"
  CoarseView = false
  Direction = (0.57735,-0.57735,0.57735)
  Focus = 100
  HardHidden = false
  IsoCount = 0
  IsoHidden = false
  IsoVisible = false
  LockPosition = false
  Perspective = false
  Rotation = 0
  RotationVector = (1,0,0)
  Scale = 0.075
  ScaleType = 2
  SeamHidden = false
  SeamVisible = true
  SmoothHidden = false
  SmoothVisible = true
  Source = -> [Pad003]
  Type = 7
  X = -69.0937
  XDirection = (0.707107,0.707107,0)
  Y = -80.2188
FEATURE [TechDraw::DrawProjGroupItem] ProjItem034  label="FrontTopLeft003"
  CoarseView = false
  Direction = (-0.57735,-0.57735,0.57735)
  Focus = 100
  HardHidden = false
  IsoCount = 0
  IsoHidden = false
  IsoVisible = false
  LockPosition = false
  Perspective = false
  Rotation = 0
  RotationVector = (1,0,0)
  Scale = 0.075
  ScaleType = 2
  SeamHidden = false
  SeamVisible = true
  SmoothHidden = false
  SmoothVisible = true
  Source = -> [Pad003]
  Type = 6
  X = 69.0937
  XDirection = (0.707107,-0.707107,0)
  Y = -80.2188
FEATURE [TechDraw::DrawProjGroupItem] ProjItem035  label="FrontBottomRight003"
  CoarseView = false
  Direction = (0.57735,-0.57735,-0.57735)
  Focus = 100
  HardHidden = false
  IsoCount = 0
  IsoHidden = false
  IsoVisible = false
  LockPosition = false
  Perspective = false
  Rotation = 0
  RotationVector = (1,0,0)
  Scale = 0.075
  ScaleType = 2
  SeamHidden = false
  SeamVisible = true
  SmoothHidden = false
  SmoothVisible = true
  Source = -> [Pad003]
  Type = 9
  X = -69.0937
  XDirection = (0.707107,0.707107,0)
  Y = 57.9685
FEATURE [TechDraw::DrawProjGroup] ProjGroup_fixed_top_part001
  Anchor = -> ProjItem027
  AutoDistribute = true
  LockPosition = false
  ProjectionType = 0
  Rotation = 0
  Scale = 0.075
  ScaleType = 1
  Source = -> [Pad003]
  Views = -> [ProjItem027,ProjItem028,ProjItem029,ProjItem030,ProjItem031,ProjItem032,ProjItem033,ProjItem034,ProjItem035]
  X = 148.5
  Y = 105
  spacingX = 15
  spacingY = 15
FEATURE [TechDraw::DrawSVGTemplate] Template_back_side001
  Height = 210
  Orientation = 1
  Width = 297
FEATURE [TechDraw::DrawProjGroupItem] ProjItem036  label="Front004"
  CoarseView = false
  Direction = (0,-1,0)
  Focus = 100
  HardHidden = false
  IsoCount = 0
  IsoHidden = false
  IsoVisible = false
  LockPosition = true
  Perspective = false
  Rotation = 0
  RotationVector = (1,0,0)
  Scale = 0.05
  ScaleType = 2
  SeamHidden = false
  SeamVisible = true
  SmoothHidden = false
  SmoothVisible = true
  Source = -> [Pad006]
  Type = 0
  X = 0
  XDirection = (1,0,0)
  Y = 0
FEATURE [TechDraw::DrawProjGroupItem] ProjItem037  label="Right004"
  CoarseView = false
  Direction = (1,-1e-16,0)
  Focus = 100
  HardHidden = false
  IsoCount = 0
  IsoHidden = false
  IsoVisible = false
  LockPosition = false
  Perspective = false
  Rotation = 0
  RotationVector = (1,0,0)
  Scale = 0.05
  ScaleType = 2
  SeamHidden = false
  SeamVisible = true
  SmoothHidden = false
  SmoothVisible = true
  Source = -> [Pad006]
  Type = 2
  X = -50
  XDirection = (1e-16,1,0)
  Y = 0
FEATURE [TechDraw::DrawProjGroupItem] ProjItem038  label="Top004"
  CoarseView = false
  Direction = (0,0,1)
  Focus = 100
  HardHidden = false
  IsoCount = 0
  IsoHidden = false
  IsoVisible = false
  LockPosition = false
  Perspective = false
  Rotation = 0
  RotationVector = (1,0,0)
  Scale = 0.05
  ScaleType = 2
  SeamHidden = false
  SeamVisible = true
  SmoothHidden = false
  SmoothVisible = true
  Source = -> [Pad006]
  Type = 4
  X = 0
  XDirection = (1,0,0)
  Y = -50
FEATURE [TechDraw::DrawProjGroupItem] ProjItem039  label="Left004"
  CoarseView = false
  Direction = (-1,-1e-16,0)
  Focus = 100
  HardHidden = false
  IsoCount = 0
  IsoHidden = false
  IsoVisible = false
  LockPosition = false
  Perspective = false
  Rotation = 0
  RotationVector = (1,0,0)
  Scale = 0.05
  ScaleType = 2
  SeamHidden = false
  SeamVisible = true
  SmoothHidden = false
  SmoothVisible = true
  Source = -> [Pad006]
  Type = 1
  X = 50
  XDirection = (1e-16,-1,0)
  Y = 0
FEATURE [TechDraw::DrawProjGroupItem] ProjItem040  label="Bottom004"
  CoarseView = false
  Direction = (0,0,-1)
  Focus = 100
  HardHidden = false
  IsoCount = 0
  IsoHidden = false
  IsoVisible = false
  LockPosition = false
  Perspective = false
  Rotation = 0
  RotationVector = (1,0,0)
  Scale = 0.05
  ScaleType = 2
  SeamHidden = false
  SeamVisible = true
  SmoothHidden = false
  SmoothVisible = true
  Source = -> [Pad006]
  Type = 5
  X = 0
  XDirection = (1,0,0)
  Y = 50
FEATURE [TechDraw::DrawProjGroupItem] ProjItem041  label="FrontBottomLeft004"
  CoarseView = false
  Direction = (-0.57735,-0.57735,-0.57735)
  Focus = 100
  HardHidden = false
  IsoCount = 0
  IsoHidden = false
  IsoVisible = false
  LockPosition = false
  Perspective = false
  Rotation = 0
  RotationVector = (1,0,0)
  Scale = 0.05
  ScaleType = 2
  SeamHidden = false
  SeamVisible = true
  SmoothHidden = false
  SmoothVisible = true
  Source = -> [Pad006]
  Type = 8
  X = 45.0511
  XDirection = (0.707107,-0.707107,0)
  Y = 48.1155
FEATURE [TechDraw::DrawProjGroupItem] ProjItem042  label="FrontTopRight004"
  CoarseView = false
  Direction = (0.57735,-0.57735,0.57735)
  Focus = 100
  HardHidden = false
  IsoCount = 0
  IsoHidden = false
  IsoVisible = false
  LockPosition = false
  Perspective = false
  Rotation = 0
  RotationVector = (1,0,0)
  Scale = 0.05
  ScaleType = 2
  SeamHidden = false
  SeamVisible = true
  SmoothHidden = false
  SmoothVisible = true
  Source = -> [Pad006]
  Type = 7
  X = -45.0511
  XDirection = (0.707107,0.707107,0)
  Y = -51.8845
FEATURE [TechDraw::DrawProjGroupItem] ProjItem043  label="FrontTopLeft004"
  CoarseView = false
  Direction = (-0.57735,-0.57735,0.57735)
  Focus = 100
  HardHidden = false
  IsoCount = 0
  IsoHidden = false
  IsoVisible = false
  LockPosition = false
  Perspective = false
  Rotation = 0
  RotationVector = (1,0,0)
  Scale = 0.05
  ScaleType = 2
  SeamHidden = false
  SeamVisible = true
  SmoothHidden = false
  SmoothVisible = true
  Source = -> [Pad006]
  Type = 6
  X = 45.0511
  XDirection = (0.707107,-0.707107,0)
  Y = -51.8845
FEATURE [TechDraw::DrawProjGroupItem] ProjItem044  label="FrontBottomRight004"
  CoarseView = false
  Direction = (0.57735,-0.57735,-0.57735)
  Focus = 100
  HardHidden = false
  IsoCount = 0
  IsoHidden = false
  IsoVisible = false
  LockPosition = false
  Perspective = false
  Rotation = 0
  RotationVector = (1,0,0)
  Scale = 0.05
  ScaleType = 2
  SeamHidden = false
  SeamVisible = true
  SmoothHidden = false
  SmoothVisible = true
  Source = -> [Pad006]
  Type = 9
  X = -45.0511
  XDirection = (0.707107,0.707107,0)
  Y = 48.1155
FEATURE [TechDraw::DrawProjGroup] ProjGroup_back_side001
  Anchor = -> ProjItem036
  AutoDistribute = true
  LockPosition = false
  ProjectionType = 0
  Rotation = 0
  Scale = 0.05
  ScaleType = 1
  Source = -> [Pad006]
  Views = -> [ProjItem036,ProjItem037,ProjItem038,ProjItem039,ProjItem040,ProjItem041,ProjItem042,ProjItem043,ProjItem044]
  X = 148.5
  Y = 105
  spacingX = 15
  spacingY = 15
FEATURE [TechDraw::DrawSVGTemplate] Template_top_door001
  Height = 210
  Orientation = 1
  Width = 297
FEATURE [TechDraw::DrawProjGroupItem] ProjItem045  label="Front005"
  CoarseView = false
  Direction = (0,-1,0)
  Focus = 100
  HardHidden = false
  IsoCount = 0
  IsoHidden = false
  IsoVisible = false
  LockPosition = true
  Perspective = false
  Rotation = 0
  RotationVector = (1,0,0)
  Scale = 0.075
  ScaleType = 2
  SeamHidden = false
  SeamVisible = true
  SmoothHidden = false
  SmoothVisible = true
  Source = -> [Pocket]
  Type = 0
  X = 0
  XDirection = (1,0,0)
  Y = 0
FEATURE [TechDraw::DrawProjGroupItem] ProjItem046  label="Right005"
  CoarseView = false
  Direction = (1,-1e-16,0)
  Focus = 100
  HardHidden = false
  IsoCount = 0
  IsoHidden = false
  IsoVisible = false
  LockPosition = false
  Perspective = false
  Rotation = 0
  RotationVector = (1,0,0)
  Scale = 0.075
  ScaleType = 2
  SeamHidden = false
  SeamVisible = true
  SmoothHidden = false
  SmoothVisible = true
  Source = -> [Pocket]
  Type = 2
  X = -74.8805
  XDirection = (1e-16,1,0)
  Y = 0
FEATURE [TechDraw::DrawProjGroupItem] ProjItem047  label="Top005"
  CoarseView = false
  Direction = (0,0,1)
  Focus = 100
  HardHidden = false
  IsoCount = 0
  IsoHidden = false
  IsoVisible = false
  LockPosition = false
  Perspective = false
  Rotation = 0
  RotationVector = (1,0,0)
  Scale = 0.075
  ScaleType = 2
  SeamHidden = false
  SeamVisible = true
  SmoothHidden = false
  SmoothVisible = true
  Source = -> [Pocket]
  Type = 4
  X = 0
  XDirection = (1,0,0)
  Y = -86.6414
FEATURE [TechDraw::DrawProjGroupItem] ProjItem048  label="Left005"
  CoarseView = false
  Direction = (-1,-1e-16,0)
  Focus = 100
  HardHidden = false
  IsoCount = 0
  IsoHidden = false
  IsoVisible = false
  LockPosition = false
  Perspective = false
  Rotation = 0
  RotationVector = (1,0,0)
  Scale = 0.075
  ScaleType = 2
  SeamHidden = false
  SeamVisible = true
  SmoothHidden = false
  SmoothVisible = true
  Source = -> [Pocket]
  Type = 1
  X = 74.8805
  XDirection = (1e-16,-1,0)
  Y = 0
FEATURE [TechDraw::DrawProjGroupItem] ProjItem049  label="Bottom005"
  CoarseView = false
  Direction = (0,0,-1)
  Focus = 100
  HardHidden = false
  IsoCount = 0
  IsoHidden = false
  IsoVisible = false
  LockPosition = false
  Perspective = false
  Rotation = 0
  RotationVector = (1,0,0)
  Scale = 0.075
  ScaleType = 2
  SeamHidden = false
  SeamVisible = true
  SmoothHidden = false
  SmoothVisible = true
  Source = -> [Pocket]
  Type = 5
  X = 0
  XDirection = (1,0,0)
  Y = 74.8805
FEATURE [TechDraw::DrawProjGroupItem] ProjItem050  label="FrontBottomLeft005"
  CoarseView = false
  Direction = (-0.57735,-0.57735,-0.57735)
  Focus = 100
  HardHidden = false
  IsoCount = 0
  IsoHidden = false
  IsoVisible = false
  LockPosition = false
  Perspective = false
  Rotation = 0
  RotationVector = (1,0,0)
  Scale = 0.075
  ScaleType = 2
  SeamHidden = false
  SeamVisible = true
  SmoothHidden = false
  SmoothVisible = true
  Source = -> [Pocket]
  Type = 8
  X = 80.7609
  XDirection = (0.707107,-0.707107,0)
  Y = 67.1702
FEATURE [TechDraw::DrawProjGroupItem] ProjItem051  label="FrontTopRight005"
  CoarseView = false
  Direction = (0.57735,-0.57735,0.57735)
  Focus = 100
  HardHidden = false
  IsoCount = 0
  IsoHidden = false
  IsoVisible = false
  LockPosition = false
  Perspective = false
  Rotation = 0
  RotationVector = (1,0,0)
  Scale = 0.075
  ScaleType = 2
  SeamHidden = false
  SeamVisible = true
  SmoothHidden = false
  SmoothVisible = true
  Source = -> [Pocket]
  Type = 7
  X = -80.7609
  XDirection = (0.707107,0.707107,0)
  Y = -94.3517
FEATURE [TechDraw::DrawProjGroupItem] ProjItem052  label="FrontTopLeft005"
  CoarseView = false
  Direction = (-0.57735,-0.57735,0.57735)
  Focus = 100
  HardHidden = false
  IsoCount = 0
  IsoHidden = false
  IsoVisible = false
  LockPosition = false
  Perspective = false
  Rotation = 0
  RotationVector = (1,0,0)
  Scale = 0.075
  ScaleType = 2
  SeamHidden = false
  SeamVisible = true
  SmoothHidden = false
  SmoothVisible = true
  Source = -> [Pocket]
  Type = 6
  X = 80.7609
  XDirection = (0.707107,-0.707107,0)
  Y = -94.3517
FEATURE [TechDraw::DrawProjGroupItem] ProjItem053  label="FrontBottomRight005"
  CoarseView = false
  Direction = (0.57735,-0.57735,-0.57735)
  Focus = 100
  HardHidden = false
  IsoCount = 0
  IsoHidden = false
  IsoVisible = false
  LockPosition = false
  Perspective = false
  Rotation = 0
  RotationVector = (1,0,0)
  Scale = 0.075
  ScaleType = 2
  SeamHidden = false
  SeamVisible = true
  SmoothHidden = false
  SmoothVisible = true
  Source = -> [Pocket]
  Type = 9
  X = -80.7609
  XDirection = (0.707107,0.707107,0)
  Y = 67.1702
FEATURE [TechDraw::DrawProjGroup] ProjGroup_top_door001
  Anchor = -> ProjItem045
  AutoDistribute = true
  LockPosition = false
  ProjectionType = 0
  Rotation = 0
  Scale = 0.075
  ScaleType = 1
  Source = -> [Pocket]
  Views = -> [ProjItem045,ProjItem046,ProjItem047,ProjItem048,ProjItem049,ProjItem050,ProjItem051,ProjItem052,ProjItem053]
  X = 148.5
  Y = 105
  spacingX = 15
  spacingY = 15
FEATURE [TechDraw::DrawSVGTemplate] Template_front_door001
  Height = 210
  Orientation = 1
  Width = 297
FEATURE [TechDraw::DrawProjGroupItem] ProjItem054  label="Front006"
  CoarseView = false
  Direction = (0,-1,0)
  Focus = 100
  HardHidden = false
  IsoCount = 0
  IsoHidden = false
  IsoVisible = false
  LockPosition = true
  Perspective = false
  Rotation = 0
  RotationVector = (1,0,0)
  Scale = 0.05
  ScaleType = 2
  SeamHidden = false
  SeamVisible = true
  SmoothHidden = false
  SmoothVisible = true
  Source = -> [Pocket001]
  Type = 0
  X = 0
  XDirection = (1,0,0)
  Y = 0
FEATURE [TechDraw::DrawProjGroupItem] ProjItem055  label="Right006"
  CoarseView = false
  Direction = (1,-1e-16,0)
  Focus = 100
  HardHidden = false
  IsoCount = 0
  IsoHidden = false
  IsoVisible = false
  LockPosition = false
  Perspective = false
  Rotation = 0
  RotationVector = (1,0,0)
  Scale = 0.05
  ScaleType = 2
  SeamHidden = false
  SeamVisible = true
  SmoothHidden = false
  SmoothVisible = true
  Source = -> [Pocket001]
  Type = 2
  X = -50
  XDirection = (1e-16,1,0)
  Y = 0
FEATURE [TechDraw::DrawProjGroupItem] ProjItem056  label="Top006"
  CoarseView = false
  Direction = (0,0,1)
  Focus = 100
  HardHidden = false
  IsoCount = 0
  IsoHidden = false
  IsoVisible = false
  LockPosition = false
  Perspective = false
  Rotation = 0
  RotationVector = (1,0,0)
  Scale = 0.05
  ScaleType = 2
  SeamHidden = false
  SeamVisible = true
  SmoothHidden = false
  SmoothVisible = true
  Source = -> [Pocket001]
  Type = 4
  X = 0
  XDirection = (1,0,0)
  Y = -50
FEATURE [TechDraw::DrawProjGroupItem] ProjItem057  label="Left006"
  CoarseView = false
  Direction = (-1,-1e-16,0)
  Focus = 100
  HardHidden = false
  IsoCount = 0
  IsoHidden = false
  IsoVisible = false
  LockPosition = false
  Perspective = false
  Rotation = 0
  RotationVector = (1,0,0)
  Scale = 0.05
  ScaleType = 2
  SeamHidden = false
  SeamVisible = true
  SmoothHidden = false
  SmoothVisible = true
  Source = -> [Pocket001]
  Type = 1
  X = 50
  XDirection = (1e-16,-1,0)
  Y = 0
FEATURE [TechDraw::DrawProjGroupItem] ProjItem058  label="Bottom006"
  CoarseView = false
  Direction = (0,0,-1)
  Focus = 100
  HardHidden = false
  IsoCount = 0
  IsoHidden = false
  IsoVisible = false
  LockPosition = false
  Perspective = false
  Rotation = 0
  RotationVector = (1,0,0)
  Scale = 0.05
  ScaleType = 2
  SeamHidden = false
  SeamVisible = true
  SmoothHidden = false
  SmoothVisible = true
  Source = -> [Pocket001]
  Type = 5
  X = 0
  XDirection = (1,0,0)
  Y = 50
FEATURE [TechDraw::DrawProjGroupItem] ProjItem059  label="FrontBottomLeft006"
  CoarseView = false
  Direction = (-0.57735,-0.57735,-0.57735)
  Focus = 100
  HardHidden = false
  IsoCount = 0
  IsoHidden = false
  IsoVisible = false
  LockPosition = false
  Perspective = false
  Rotation = 0
  RotationVector = (1,0,0)
  Scale = 0.05
  ScaleType = 2
  SeamHidden = false
  SeamVisible = true
  SmoothHidden = false
  SmoothVisible = true
  Source = -> [Pocket001]
  Type = 8
  X = 45.0511
  XDirection = (0.707107,-0.707107,0)
  Y = 48.1155
FEATURE [TechDraw::DrawProjGroupItem] ProjItem060  label="FrontTopRight006"
  CoarseView = false
  Direction = (0.57735,-0.57735,0.57735)
  Focus = 100
  HardHidden = false
  IsoCount = 0
  IsoHidden = false
  IsoVisible = false
  LockPosition = false
  Perspective = false
  Rotation = 0
  RotationVector = (1,0,0)
  Scale = 0.05
  ScaleType = 2
  SeamHidden = false
  SeamVisible = true
  SmoothHidden = false
  SmoothVisible = true
  Source = -> [Pocket001]
  Type = 7
  X = -45.0511
  XDirection = (0.707107,0.707107,0)
  Y = -51.8845
FEATURE [TechDraw::DrawProjGroupItem] ProjItem061  label="FrontTopLeft006"
  CoarseView = false
  Direction = (-0.57735,-0.57735,0.57735)
  Focus = 100
  HardHidden = false
  IsoCount = 0
  IsoHidden = false
  IsoVisible = false
  LockPosition = false
  Perspective = false
  Rotation = 0
  RotationVector = (1,0,0)
  Scale = 0.05
  ScaleType = 2
  SeamHidden = false
  SeamVisible = true
  SmoothHidden = false
  SmoothVisible = true
  Source = -> [Pocket001]
  Type = 6
  X = 45.0511
  XDirection = (0.707107,-0.707107,0)
  Y = -51.8845
FEATURE [TechDraw::DrawProjGroupItem] ProjItem062  label="FrontBottomRight006"
  CoarseView = false
  Direction = (0.57735,-0.57735,-0.57735)
  Focus = 100
  HardHidden = false
  IsoCount = 0
  IsoHidden = false
  IsoVisible = false
  LockPosition = false
  Perspective = false
  Rotation = 0
  RotationVector = (1,0,0)
  Scale = 0.05
  ScaleType = 2
  SeamHidden = false
  SeamVisible = true
  SmoothHidden = false
  SmoothVisible = true
  Source = -> [Pocket001]
  Type = 9
  X = -45.0511
  XDirection = (0.707107,0.707107,0)
  Y = 48.1155
FEATURE [TechDraw::DrawProjGroup] ProjGroup_front_door001
  Anchor = -> ProjItem054
  AutoDistribute = true
  LockPosition = false
  ProjectionType = 0
  Rotation = 0
  Scale = 0.05
  ScaleType = 1
  Source = -> [Pocket001]
  Views = -> [ProjItem054,ProjItem055,ProjItem056,ProjItem057,ProjItem058,ProjItem059,ProjItem060,ProjItem061,ProjItem062]
  X = 148.5
  Y = 105
  spacingX = 15
  spacingY = 15
FEATURE [TechDraw::DrawSVGTemplate] Template_top_glass001
  Height = 210
  Orientation = 1
  Width = 297
FEATURE [TechDraw::DrawProjGroupItem] ProjItem063  label="Front007"
  CoarseView = false
  Direction = (0,-1,0)
  Focus = 100
  HardHidden = false
  IsoCount = 0
  IsoHidden = false
  IsoVisible = false
  LockPosition = true
  Perspective = false
  Rotation = 0
  RotationVector = (1,0,0)
  Scale = 0.1
  ScaleType = 2
  SeamHidden = false
  SeamVisible = true
  SmoothHidden = false
  SmoothVisible = true
  Source = -> [Pad007]
  Type = 0
  X = 0
  XDirection = (1,0,0)
  Y = 0
FEATURE [TechDraw::DrawProjGroupItem] ProjItem064  label="Right007"
  CoarseView = false
  Direction = (1,-1e-16,0)
  Focus = 100
  HardHidden = false
  IsoCount = 0
  IsoHidden = false
  IsoVisible = false
  LockPosition = false
  Perspective = false
  Rotation = 0
  RotationVector = (1,0,0)
  Scale = 0.1
  ScaleType = 2
  SeamHidden = false
  SeamVisible = true
  SmoothHidden = false
  SmoothVisible = true
  Source = -> [Pad007]
  Type = 2
  X = -80.3553
  XDirection = (1e-16,1,0)
  Y = 0
FEATURE [TechDraw::DrawProjGroupItem] ProjItem065  label="Top007"
  CoarseView = false
  Direction = (0,0,1)
  Focus = 100
  HardHidden = false
  IsoCount = 0
  IsoHidden = false
  IsoVisible = false
  LockPosition = false
  Perspective = false
  Rotation = 0
  RotationVector = (1,0,0)
  Scale = 0.1
  ScaleType = 2
  SeamHidden = false
  SeamVisible = true
  SmoothHidden = false
  SmoothVisible = true
  Source = -> [Pad007]
  Type = 4
  X = 0
  XDirection = (1,0,0)
  Y = -91.066
FEATURE [TechDraw::DrawProjGroupItem] ProjItem066  label="Left007"
  CoarseView = false
  Direction = (-1,-1e-16,0)
  Focus = 100
  HardHidden = false
  IsoCount = 0
  IsoHidden = false
  IsoVisible = false
  LockPosition = false
  Perspective = false
  Rotation = 0
  RotationVector = (1,0,0)
  Scale = 0.1
  ScaleType = 2
  SeamHidden = false
  SeamVisible = true
  SmoothHidden = false
  SmoothVisible = true
  Source = -> [Pad007]
  Type = 1
  X = 80.3553
  XDirection = (1e-16,-1,0)
  Y = 0
FEATURE [TechDraw::DrawProjGroupItem] ProjItem067  label="Bottom007"
  CoarseView = false
  Direction = (0,0,-1)
  Focus = 100
  HardHidden = false
  IsoCount = 0
  IsoHidden = false
  IsoVisible = false
  LockPosition = false
  Perspective = false
  Rotation = 0
  RotationVector = (1,0,0)
  Scale = 0.1
  ScaleType = 2
  SeamHidden = false
  SeamVisible = true
  SmoothHidden = false
  SmoothVisible = true
  Source = -> [Pad007]
  Type = 5
  X = 0
  XDirection = (1,0,0)
  Y = 80.3553
FEATURE [TechDraw::DrawProjGroupItem] ProjItem068  label="FrontBottomLeft007"
  CoarseView = false
  Direction = (-0.57735,-0.57735,-0.57735)
  Focus = 100
  HardHidden = false
  IsoCount = 0
  IsoHidden = false
  IsoVisible = false
  LockPosition = false
  Perspective = false
  Rotation = 0
  RotationVector = (1,0,0)
  Scale = 0.1
  ScaleType = 2
  SeamHidden = false
  SeamVisible = true
  SmoothHidden = false
  SmoothVisible = true
  Source = -> [Pad007]
  Type = 8
  X = 85.7107
  XDirection = (0.707107,-0.707107,0)
  Y = 70.9719
FEATURE [TechDraw::DrawProjGroupItem] ProjItem069  label="FrontTopRight007"
  CoarseView = false
  Direction = (0.57735,-0.57735,0.57735)
  Focus = 100
  HardHidden = false
  IsoCount = 0
  IsoHidden = false
  IsoVisible = false
  LockPosition = false
  Perspective = false
  Rotation = 0
  RotationVector = (1,0,0)
  Scale = 0.1
  ScaleType = 2
  SeamHidden = false
  SeamVisible = true
  SmoothHidden = false
  SmoothVisible = true
  Source = -> [Pad007]
  Type = 7
  X = -85.7107
  XDirection = (0.707107,0.707107,0)
  Y = -100.449
FEATURE [TechDraw::DrawProjGroupItem] ProjItem070  label="FrontTopLeft007"
  CoarseView = false
  Direction = (-0.57735,-0.57735,0.57735)
  Focus = 100
  HardHidden = false
  IsoCount = 0
  IsoHidden = false
  IsoVisible = false
  LockPosition = false
  Perspective = false
  Rotation = 0
  RotationVector = (1,0,0)
  Scale = 0.1
  ScaleType = 2
  SeamHidden = false
  SeamVisible = true
  SmoothHidden = false
  SmoothVisible = true
  Source = -> [Pad007]
  Type = 6
  X = 85.7107
  XDirection = (0.707107,-0.707107,0)
  Y = -100.449
FEATURE [TechDraw::DrawProjGroupItem] ProjItem071  label="FrontBottomRight007"
  CoarseView = false
  Direction = (0.57735,-0.57735,-0.57735)
  Focus = 100
  HardHidden = false
  IsoCount = 0
  IsoHidden = false
  IsoVisible = false
  LockPosition = false
  Perspective = false
  Rotation = 0
  RotationVector = (1,0,0)
  Scale = 0.1
  ScaleType = 2
  SeamHidden = false
  SeamVisible = true
  SmoothHidden = false
  SmoothVisible = true
  Source = -> [Pad007]
  Type = 9
  X = -85.7107
  XDirection = (0.707107,0.707107,0)
  Y = 70.9719
FEATURE [TechDraw::DrawProjGroup] ProjGroup_top_glass001
  Anchor = -> ProjItem063
  AutoDistribute = true
  LockPosition = false
  ProjectionType = 0
  Rotation = 0
  Scale = 0.1
  ScaleType = 1
  Source = -> [Pad007]
  Views = -> [ProjItem063,ProjItem064,ProjItem065,ProjItem066,ProjItem067,ProjItem068,ProjItem069,ProjItem070,ProjItem071]
  X = 148.5
  Y = 105
  spacingX = 15
  spacingY = 15
FEATURE [TechDraw::DrawSVGTemplate] Template_front_glass001
  Height = 210
  Orientation = 1
  Width = 297
FEATURE [TechDraw::DrawProjGroupItem] ProjItem072  label="Front008"
  CoarseView = false
  Direction = (0,-1,0)
  Focus = 100
  HardHidden = false
  IsoCount = 0
  IsoHidden = false
  IsoVisible = false
  LockPosition = true
  Perspective = false
  Rotation = 0
  RotationVector = (1,0,0)
  Scale = 0.1
  ScaleType = 2
  SeamHidden = false
  SeamVisible = true
  SmoothHidden = false
  SmoothVisible = true
  Source = -> [Pad008]
  Type = 0
  X = 0
  XDirection = (1,0,0)
  Y = 0
FEATURE [TechDraw::DrawProjGroupItem] ProjItem073  label="Right008"
  CoarseView = false
  Direction = (1,-1e-16,0)
  Focus = 100
  HardHidden = false
  IsoCount = 0
  IsoHidden = false
  IsoVisible = false
  LockPosition = false
  Perspective = false
  Rotation = 0
  RotationVector = (1,0,0)
  Scale = 0.1
  ScaleType = 2
  SeamHidden = false
  SeamVisible = true
  SmoothHidden = false
  SmoothVisible = true
  Source = -> [Pad008]
  Type = 2
  X = -57
  XDirection = (1e-16,1,0)
  Y = 0
FEATURE [TechDraw::DrawProjGroupItem] ProjItem074  label="Top008"
  CoarseView = false
  Direction = (0,0,1)
  Focus = 100
  HardHidden = false
  IsoCount = 0
  IsoHidden = false
  IsoVisible = false
  LockPosition = false
  Perspective = false
  Rotation = 0
  RotationVector = (1,0,0)
  Scale = 0.1
  ScaleType = 2
  SeamHidden = false
  SeamVisible = true
  SmoothHidden = false
  SmoothVisible = true
  Source = -> [Pad008]
  Type = 4
  X = 0
  XDirection = (1,0,0)
  Y = -57
FEATURE [TechDraw::DrawProjGroupItem] ProjItem075  label="Left008"
  CoarseView = false
  Direction = (-1,-1e-16,0)
  Focus = 100
  HardHidden = false
  IsoCount = 0
  IsoHidden = false
  IsoVisible = false
  LockPosition = false
  Perspective = false
  Rotation = 0
  RotationVector = (1,0,0)
  Scale = 0.1
  ScaleType = 2
  SeamHidden = false
  SeamVisible = true
  SmoothHidden = false
  SmoothVisible = true
  Source = -> [Pad008]
  Type = 1
  X = 57
  XDirection = (1e-16,-1,0)
  Y = 0
FEATURE [TechDraw::DrawProjGroupItem] ProjItem076  label="Bottom008"
  CoarseView = false
  Direction = (0,0,-1)
  Focus = 100
  HardHidden = false
  IsoCount = 0
  IsoHidden = false
  IsoVisible = false
  LockPosition = false
  Perspective = false
  Rotation = 0
  RotationVector = (1,0,0)
  Scale = 0.1
  ScaleType = 2
  SeamHidden = false
  SeamVisible = true
  SmoothHidden = false
  SmoothVisible = true
  Source = -> [Pad008]
  Type = 5
  X = 0
  XDirection = (1,0,0)
  Y = 57
FEATURE [TechDraw::DrawProjGroupItem] ProjItem077  label="FrontBottomLeft008"
  CoarseView = false
  Direction = (-0.57735,-0.57735,-0.57735)
  Focus = 100
  HardHidden = false
  IsoCount = 0
  IsoHidden = false
  IsoVisible = false
  LockPosition = false
  Perspective = false
  Rotation = 0
  RotationVector = (1,0,0)
  Scale = 0.1
  ScaleType = 2
  SeamHidden = false
  SeamVisible = true
  SmoothHidden = false
  SmoothVisible = true
  Source = -> [Pad008]
  Type = 8
  X = 51.026
  XDirection = (0.707107,-0.707107,0)
  Y = 55.698
FEATURE [TechDraw::DrawProjGroupItem] ProjItem078  label="FrontTopRight008"
  CoarseView = false
  Direction = (0.57735,-0.57735,0.57735)
  Focus = 100
  HardHidden = false
  IsoCount = 0
  IsoHidden = false
  IsoVisible = false
  LockPosition = false
  Perspective = false
  Rotation = 0
  RotationVector = (1,0,0)
  Scale = 0.1
  ScaleType = 2
  SeamHidden = false
  SeamVisible = true
  SmoothHidden = false
  SmoothVisible = true
  Source = -> [Pad008]
  Type = 7
  X = -51.026
  XDirection = (0.707107,0.707107,0)
  Y = -58.302
FEATURE [TechDraw::DrawProjGroupItem] ProjItem079  label="FrontTopLeft008"
  CoarseView = false
  Direction = (-0.57735,-0.57735,0.57735)
  Focus = 100
  HardHidden = false
  IsoCount = 0
  IsoHidden = false
  IsoVisible = false
  LockPosition = false
  Perspective = false
  Rotation = 0
  RotationVector = (1,0,0)
  Scale = 0.1
  ScaleType = 2
  SeamHidden = false
  SeamVisible = true
  SmoothHidden = false
  SmoothVisible = true
  Source = -> [Pad008]
  Type = 6
  X = 51.026
  XDirection = (0.707107,-0.707107,0)
  Y = -58.302
FEATURE [TechDraw::DrawProjGroupItem] ProjItem080  label="FrontBottomRight008"
  CoarseView = false
  Direction = (0.57735,-0.57735,-0.57735)
  Focus = 100
  HardHidden = false
  IsoCount = 0
  IsoHidden = false
  IsoVisible = false
  LockPosition = false
  Perspective = false
  Rotation = 0
  RotationVector = (1,0,0)
  Scale = 0.1
  ScaleType = 2
  SeamHidden = false
  SeamVisible = true
  SmoothHidden = false
  SmoothVisible = true
  Source = -> [Pad008]
  Type = 9
  X = -51.026
  XDirection = (0.707107,0.707107,0)
  Y = 55.698
FEATURE [TechDraw::DrawProjGroup] ProjGroup_front_glass001
  Anchor = -> ProjItem072
  AutoDistribute = true
  LockPosition = false
  ProjectionType = 0
  Rotation = 0
  Scale = 0.1
  ScaleType = 1
  Source = -> [Pad008]
  Views = -> [ProjItem072,ProjItem073,ProjItem074,ProjItem075,ProjItem076,ProjItem077,ProjItem078,ProjItem079,ProjItem080]
  X = 148.5
  Y = 105
  spacingX = 15
  spacingY = 15
FEATURE [TechDraw::DrawViewDimension] Dimension
  Arbitrary = false
  ArbitraryTolerances = false
  EqualTolerance = true
  FormatSpec = %.2f
  FormatSpecOverTolerance = %+.2f
  FormatSpecUnderTolerance = %+.2f
  Inverted = false
  LockPosition = false
  MeasureType = 1
  OverTolerance = 0
  References2D = -> [ProjItem049]
  Rotation = 0
  ScaleType = 0
  TheoreticalExact = false
  Type = 2
  UnderTolerance = 0
  X = 25.9657
  Y = -0.380334
FEATURE [TechDraw::DrawViewDimension] Dimension001
  Arbitrary = false
  ArbitraryTolerances = false
  EqualTolerance = true
  FormatSpec = %.2f
  FormatSpecOverTolerance = %+.2f
  FormatSpecUnderTolerance = %+.2f
  Inverted = false
  LockPosition = false
  MeasureType = 1
  OverTolerance = 0
  References2D = -> [ProjItem049]
  Rotation = 0
  ScaleType = 0
  TheoreticalExact = false
  Type = 1
  UnderTolerance = 0
  X = 0
  Y = 45.0659
FEATURE [TechDraw::DrawViewDimension] Dimension002
  Arbitrary = false
  ArbitraryTolerances = false
  EqualTolerance = true
  FormatSpec = %.2f
  FormatSpecOverTolerance = %+.2f
  FormatSpecUnderTolerance = %+.2f
  Inverted = false
  LockPosition = false
  MeasureType = 1
  OverTolerance = 0
  References2D = -> [ProjItem049]
  Rotation = 0
  ScaleType = 0
  TheoreticalExact = false
  Type = 1
  UnderTolerance = 0
  X = -28.4752
  Y = -33.5163
FEATURE [TechDraw::DrawViewDimension] Dimension003
  Arbitrary = false
  ArbitraryTolerances = false
  EqualTolerance = true
  FormatSpec = %.2f
  FormatSpecOverTolerance = %+.2f
  FormatSpecUnderTolerance = %+.2f
  Inverted = false
  LockPosition = false
  MeasureType = 1
  OverTolerance = 0
  References2D = -> [ProjItem049]
  Rotation = 0
  ScaleType = 0
  TheoreticalExact = false
  Type = 2
  UnderTolerance = 0
  X = -34.0034
  Y = 36.7358
FEATURE [TechDraw::DrawViewDimension] Dimension004
  Arbitrary = false
  ArbitraryTolerances = false
  EqualTolerance = true
  FormatSpec = R%.2f
  FormatSpecOverTolerance = %+.2f
  FormatSpecUnderTolerance = %+.2f
  Inverted = false
  LockPosition = false
  MeasureType = 1
  OverTolerance = 0
  References2D = -> [ProjItem049]
  Rotation = 0
  ScaleType = 0
  TheoreticalExact = false
  Type = 4
  UnderTolerance = 0
  X = -35.7281
  Y = -14.0747
FEATURE [TechDraw::DrawPage] Page_top_door001
  KeepUpdated = true
  NextBalloonIndex = 1
  ProjectionType = 0
  Template = -> Template_top_door001
  Views = -> [ProjGroup_top_door001,Dimension,Dimension001,Dimension002,Dimension003,Dimension004]
FEATURE [TechDraw::DrawViewDimension] Dimension005
  Arbitrary = false
  ArbitraryTolerances = false
  EqualTolerance = true
  FormatSpec = %.2f
  FormatSpecOverTolerance = %+.2f
  FormatSpecUnderTolerance = %+.2f
  Inverted = false
  LockPosition = false
  MeasureType = 1
  OverTolerance = 0
  References2D = -> [ProjItem004]
  Rotation = 0
  ScaleType = 0
  TheoreticalExact = false
  Type = 2
  UnderTolerance = 0
  X = 26.425
  Y = 0
FEATURE [TechDraw::DrawViewDimension] Dimension006
  Arbitrary = false
  ArbitraryTolerances = false
  EqualTolerance = true
  FormatSpec = %.2f
  FormatSpecOverTolerance = %+.2f
  FormatSpecUnderTolerance = %+.2f
  Inverted = false
  LockPosition = false
  MeasureType = 1
  OverTolerance = 0
  References2D = -> [ProjItem004]
  Rotation = 0
  ScaleType = 0
  TheoreticalExact = false
  Type = 1
  UnderTolerance = 0
  X = -0.658333
  Y = 30.5083
FEATURE [TechDraw::DrawPage] Page_bottom001
  KeepUpdated = true
  NextBalloonIndex = 1
  ProjectionType = 0
  Template = -> Template_bottom001
  Views = -> [ProjGroup_bottom001,Dimension005,Dimension006]
FEATURE [TechDraw::DrawViewDimension] Dimension007
  Arbitrary = false
  ArbitraryTolerances = false
  EqualTolerance = true
  FormatSpec = %.2f
  FormatSpecOverTolerance = %+.2f
  FormatSpecUnderTolerance = %+.2f
  Inverted = false
  LockPosition = false
  MeasureType = 1
  OverTolerance = 0
  References2D = -> [ProjItem009]
  Rotation = 0
  ScaleType = 0
  TheoreticalExact = false
  Type = 2
  UnderTolerance = 0
  X = -42.8327
  Y = -1.03566
FEATURE [TechDraw::DrawViewDimension] Dimension008
  Arbitrary = false
  ArbitraryTolerances = false
  EqualTolerance = true
  FormatSpec = %.2f
  FormatSpecOverTolerance = %+.2f
  FormatSpecUnderTolerance = %+.2f
  Inverted = false
  LockPosition = false
  MeasureType = 1
  OverTolerance = 0
  References2D = -> [ProjItem009]
  Rotation = 0
  ScaleType = 0
  TheoreticalExact = false
  Type = 1
  UnderTolerance = 0
  X = -0.69044
  Y = -20.8985
FEATURE [TechDraw::DrawPage] Page_right_side001
  KeepUpdated = true
  NextBalloonIndex = 1
  ProjectionType = 0
  Template = -> Template_right_side001
  Views = -> [ProjGroup_right_side001,Dimension007,Dimension008]
FEATURE [TechDraw::DrawViewDimension] Dimension009
  Arbitrary = false
  ArbitraryTolerances = false
  EqualTolerance = true
  FormatSpec = %.2f
  FormatSpecOverTolerance = %+.2f
  FormatSpecUnderTolerance = %+.2f
  Inverted = false
  LockPosition = false
  MeasureType = 1
  OverTolerance = 0
  References2D = -> [ProjItem018]
  Rotation = 0
  ScaleType = 0
  TheoreticalExact = false
  Type = 1
  UnderTolerance = 0
  X = -1.38088
  Y = -22.6246
FEATURE [TechDraw::DrawViewDimension] Dimension010
  Arbitrary = false
  ArbitraryTolerances = false
  EqualTolerance = true
  FormatSpec = %.2f
  FormatSpecOverTolerance = %+.2f
  FormatSpecUnderTolerance = %+.2f
  Inverted = false
  LockPosition = false
  MeasureType = 1
  OverTolerance = 0
  References2D = -> [ProjItem018]
  Rotation = 0
  ScaleType = 0
  TheoreticalExact = false
  Type = 2
  UnderTolerance = 0
  X = -37.9996
  Y = 0
FEATURE [TechDraw::DrawPage] Page_left_side001
  KeepUpdated = true
  NextBalloonIndex = 1
  ProjectionType = 0
  Template = -> Template_left_side001
  Views = -> [ProjGroup_left_side001,Dimension009,Dimension010]
FEATURE [TechDraw::DrawViewDimension] Dimension011
  Arbitrary = false
  ArbitraryTolerances = false
  EqualTolerance = true
  FormatSpec = %.2f
  FormatSpecOverTolerance = %+.2f
  FormatSpecUnderTolerance = %+.2f
  Inverted = false
  LockPosition = false
  MeasureType = 1
  OverTolerance = 0
  References2D = -> [ProjItem031]
  Rotation = 0
  ScaleType = 0
  TheoreticalExact = false
  Type = 2
  UnderTolerance = 0
  X = 21.5056
  Y = -0.813201
FEATURE [TechDraw::DrawViewDimension] Dimension012
  Arbitrary = false
  ArbitraryTolerances = false
  EqualTolerance = true
  FormatSpec = %.2f
  FormatSpecOverTolerance = %+.2f
  FormatSpecUnderTolerance = %+.2f
  Inverted = false
  LockPosition = false
  MeasureType = 1
  OverTolerance = 0
  References2D = -> [ProjItem031]
  Rotation = 0
  ScaleType = 0
  TheoreticalExact = false
  Type = 1
  UnderTolerance = 0
  X = 0
  Y = -44.132
FEATURE [TechDraw::DrawPage] Page_fixed_top_part001
  KeepUpdated = true
  NextBalloonIndex = 1
  ProjectionType = 0
  Template = -> Template_fixed_top_part001
  Views = -> [ProjGroup_fixed_top_part001,Dimension011,Dimension012]
FEATURE [TechDraw::DrawViewDimension] Dimension013
  Arbitrary = false
  ArbitraryTolerances = false
  EqualTolerance = true
  FormatSpec = %.2f
  FormatSpecOverTolerance = %+.2f
  FormatSpecUnderTolerance = %+.2f
  Inverted = false
  LockPosition = false
  MeasureType = 1
  OverTolerance = 0
  References2D = -> [ProjItem037]
  Rotation = 0
  ScaleType = 0
  TheoreticalExact = false
  Type = 1
  UnderTolerance = 0
  X = -1.94841
  Y = 29.3386
FEATURE [TechDraw::DrawViewDimension] Dimension014
  Arbitrary = false
  ArbitraryTolerances = false
  EqualTolerance = true
  FormatSpec = %.2f
  FormatSpecOverTolerance = %+.2f
  FormatSpecUnderTolerance = %+.2f
  Inverted = false
  LockPosition = false
  MeasureType = 1
  OverTolerance = 0
  References2D = -> [ProjItem037]
  Rotation = 0
  ScaleType = 0
  TheoreticalExact = false
  Type = 2
  UnderTolerance = 0
  X = 32.7447
  Y = -0.324734
FEATURE [TechDraw::DrawPage] Page_back_side001
  KeepUpdated = true
  NextBalloonIndex = 1
  ProjectionType = 0
  Template = -> Template_back_side001
  Views = -> [ProjGroup_back_side001,Dimension013,Dimension014]
FEATURE [TechDraw::DrawViewDimension] Dimension015
  Arbitrary = false
  ArbitraryTolerances = false
  EqualTolerance = true
  FormatSpec = %.2f
  FormatSpecOverTolerance = %+.2f
  FormatSpecUnderTolerance = %+.2f
  Inverted = false
  LockPosition = false
  MeasureType = 1
  OverTolerance = 0
  References2D = -> [ProjItem057]
  Rotation = 0
  ScaleType = 0
  TheoreticalExact = false
  Type = 1
  UnderTolerance = 0
  X = -0.343103
  Y = 26.1827
FEATURE [TechDraw::DrawViewDimension] Dimension016
  Arbitrary = false
  ArbitraryTolerances = false
  EqualTolerance = true
  FormatSpec = %.2f
  FormatSpecOverTolerance = %+.2f
  FormatSpecUnderTolerance = %+.2f
  Inverted = false
  LockPosition = false
  MeasureType = 1
  OverTolerance = 0
  References2D = -> [ProjItem057]
  Rotation = 0
  ScaleType = 0
  TheoreticalExact = false
  Type = 2
  UnderTolerance = 0
  X = 33.1121
  Y = -0.171551
FEATURE [TechDraw::DrawViewDimension] Dimension017
  Arbitrary = false
  ArbitraryTolerances = false
  EqualTolerance = true
  FormatSpec = %.2f
  FormatSpecOverTolerance = %+.2f
  FormatSpecUnderTolerance = %+.2f
  Inverted = false
  LockPosition = false
  MeasureType = 1
  OverTolerance = 0
  References2D = -> [ProjItem057]
  Rotation = 0
  ScaleType = 0
  TheoreticalExact = false
  Type = 2
  UnderTolerance = 0
  X = -43.8762
  Y = -23.8689
FEATURE [TechDraw::DrawViewDimension] Dimension018
  Arbitrary = false
  ArbitraryTolerances = false
  EqualTolerance = true
  FormatSpec = %.2f
  FormatSpecOverTolerance = %+.2f
  FormatSpecUnderTolerance = %+.2f
  Inverted = false
  LockPosition = false
  MeasureType = 1
  OverTolerance = 0
  References2D = -> [ProjItem057]
  Rotation = 0
  ScaleType = 0
  TheoreticalExact = false
  Type = 1
  UnderTolerance = 0
  X = 19.5159
  Y = -26.4422
FEATURE [TechDraw::DrawPage] Page_front_door001
  KeepUpdated = true
  NextBalloonIndex = 1
  ProjectionType = 0
  Template = -> Template_front_door001
  Views = -> [ProjGroup_front_door001,Dimension015,Dimension016,Dimension017,Dimension018]
FEATURE [TechDraw::DrawViewDimension] Dimension019
  Arbitrary = false
  ArbitraryTolerances = false
  EqualTolerance = true
  FormatSpec = %.2f
  FormatSpecOverTolerance = %+.2f
  FormatSpecUnderTolerance = %+.2f
  Inverted = false
  LockPosition = false
  MeasureType = 1
  OverTolerance = 0
  References2D = -> [ProjItem065]
  Rotation = 0
  ScaleType = 0
  TheoreticalExact = false
  Type = 2
  UnderTolerance = 0
  X = 26.9194
  Y = 1.15978
FEATURE [TechDraw::DrawViewDimension] Dimension020
  Arbitrary = false
  ArbitraryTolerances = false
  EqualTolerance = true
  FormatSpec = %.2f
  FormatSpecOverTolerance = %+.2f
  FormatSpecUnderTolerance = %+.2f
  Inverted = false
  LockPosition = false
  MeasureType = 1
  OverTolerance = 0
  References2D = -> [ProjItem065]
  Rotation = 0
  ScaleType = 0
  TheoreticalExact = false
  Type = 1
  UnderTolerance = 0
  X = -0.384099
  Y = 41.1389
FEATURE [TechDraw::DrawPage] Page_top_glass001
  KeepUpdated = true
  NextBalloonIndex = 1
  ProjectionType = 0
  Template = -> Template_top_glass001
  Views = -> [ProjGroup_top_glass001,Dimension019,Dimension020]
FEATURE [TechDraw::DrawViewDimension] Dimension021
  Arbitrary = false
  ArbitraryTolerances = false
  EqualTolerance = true
  FormatSpec = %.2f
  FormatSpecOverTolerance = %+.2f
  FormatSpecUnderTolerance = %+.2f
  Inverted = false
  LockPosition = false
  MeasureType = 1
  OverTolerance = 0
  References2D = -> [ProjItem075]
  Rotation = 0
  ScaleType = 0
  TheoreticalExact = false
  Type = 1
  UnderTolerance = 0
  X = 0
  Y = 27.2665
FEATURE [TechDraw::DrawViewDimension] Dimension022
  Arbitrary = false
  ArbitraryTolerances = false
  EqualTolerance = true
  FormatSpec = %.2f
  FormatSpecOverTolerance = %+.2f
  FormatSpecUnderTolerance = %+.2f
  Inverted = false
  LockPosition = false
  MeasureType = 1
  OverTolerance = 0
  References2D = -> [ProjItem075]
  Rotation = 0
  ScaleType = 0
  TheoreticalExact = false
  Type = 2
  UnderTolerance = 0
  X = 33.0694
  Y = 2.92261
FEATURE [TechDraw::DrawPage] Page_front_glass001
  KeepUpdated = true
  NextBalloonIndex = 1
  ProjectionType = 0
  Template = -> Template_front_glass001
  Views = -> [ProjGroup_front_glass001,Dimension021,Dimension022]
FEATURE [Sketcher::SketchObject] Sketch012
  ExternalGeometry = -> [Pad006]
  FullyConstrained = true
  MapMode = 5
  Placement = pos=(-410,0,10) rot=(0.57735,-0.57735,-0.57735;2.0944rad)
  Support = -> [Pad006]
  sketch-geometry (2):
    g0: LineSegment StartX=-350 StartY=205 StartZ=0 EndX=350 EndY=205 EndZ=0
    g1: Circle CenterX=0 CenterY=205 CenterZ=0 NormalX=0 NormalY=0 NormalZ=1 AngleXU=0 Radius=40
  constraints (6):
    c: PointOnObject(g0,g-4)
    c: Horizontal(g0)
    c: Symmetric(g-5,g-5,g0)
    c: PointOnObject(g1,g0)
    c: PointOnObject(g1,g-2)
    c: Radius(g1) = 40
FEATURE [PartDesign::Pocket] Pocket002
  BaseFeature = -> Pad006
  Length = 10
  Length2 = 100
  Placement = pos=(0,0,10) rot=(0,0,1;0rad)
  Profile = -> Sketch012
  Type = 0
FEATURE [PartDesign::Body] Body006  label="back_side"
  Group = -> [CopyPad001002,Sketch006,Pad006,Sketch012,Pocket002]
  Origin = -> Origin006
  Tip = -> Pocket002
